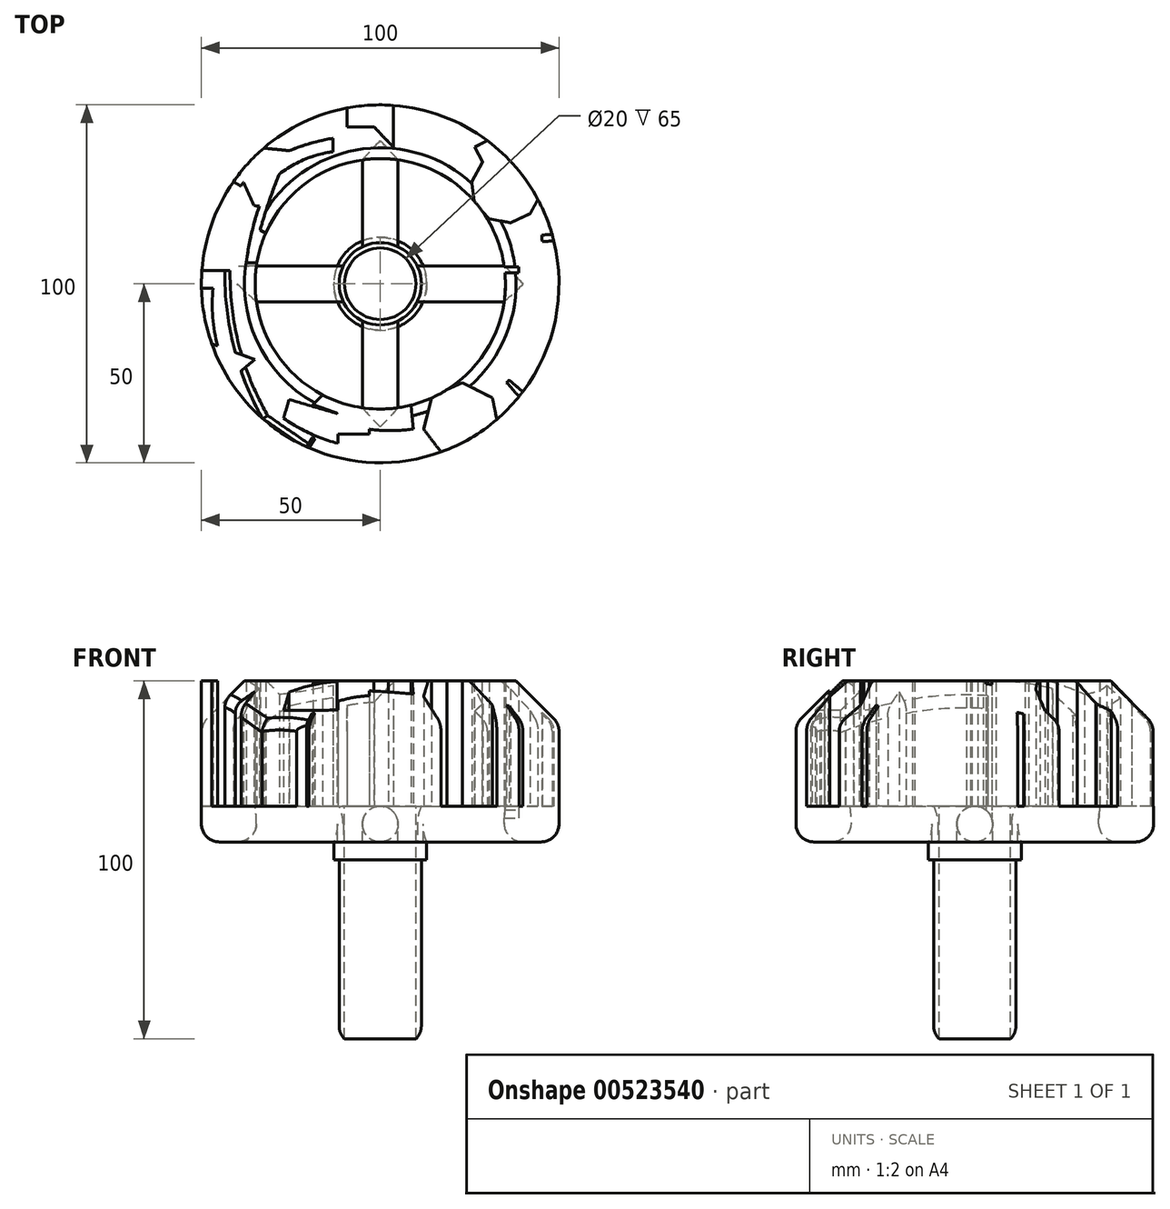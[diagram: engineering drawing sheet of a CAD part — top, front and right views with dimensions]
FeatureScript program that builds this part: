
annotation { "Feature Type Name" : "Feature", "Feature Type Description" : "" }
export const myFeature = defineFeature(function(context is Context, id is Id, definition is map)
    precondition{}
    {
        {
            var Q0;
            Q0=qCreatedBy(makeId("Top.planeOp"),FACE);
            var sketch = newSketch(context, id + "F0", { "sketchPlane" : qUnion([Q0])});
            skCircle(sketch, "E0", {"center": v(0, 0) * mm, "radius": 50 * mm});
            skArc(sketch, "E1", {"start": v(-1.78, 34.95) * mm, "mid": v(-24.53, 24.96) * mm, "end": v(-34.92, 2.39) * mm});
            skArc(sketch, "E2.trimOffspring", {"start": v(34.99, 0.84) * mm, "mid": v(25.27, 24.22) * mm, "end": v(2.33, 34.92) * mm});
            skArc(sketch, "E3.trimOffspring", {"start": v(2.06, -34.94) * mm, "mid": v(25.17, -24.32) * mm, "end": v(34.99, -0.84) * mm});
            skArc(sketch, "E4.trimOffspring", {"start": v(-34.92, -2.39) * mm, "mid": v(-24.63, -24.87) * mm, "end": v(-2.06, -34.94) * mm});
            skLineSegment(sketch, "E5", {"start": v(-2.06, -34.94) * mm, "end": v(2.06, -34.94) * mm});
            skLineSegment(sketch, "E6", {"start": v(-34.92, 2.39) * mm, "end": v(-34.92, -2.39) * mm});
            skLineSegment(sketch, "E7", {"start": v(-1.78, 34.95) * mm, "end": v(2.33, 34.92) * mm});
            skLineSegment(sketch, "E8", {"start": v(34.99, 0.84) * mm, "end": v(34.99, -0.84) * mm});
            skLineSegment(sketch, "E9", {"start": v(-49.98, -1.23) * mm, "end": v(-46.76, -1.23) * mm});
            skArc(sketch, "E10", {"start": v(-46.76, -1.23) * mm, "mid": v(-41.77, -26.37) * mm, "end": v(-23.36, -44.2) * mm});
            skLineSegment(sketch, "E11", {"start": v(-23.36, -44.2) * mm, "end": v(-33, -37.57) * mm});
            skArc(sketch, "E12", {"start": v(-43.46, 3.7) * mm, "mid": v(-40.95, -17.62) * mm, "end": v(-33, -37.57) * mm});
            skLineSegment(sketch, "E13", {"start": v(-43.46, 3.7) * mm, "end": v(-49.86, 3.7) * mm});
            skLineSegment(sketch, "E14", {"start": v(-34.5, 5.89) * mm, "end": v(-37.45, 5.89) * mm});
            skArc(sketch, "E15", {"start": v(-27.87, 34.5) * mm, "mid": v(-34.13, 20.68) * mm, "end": v(-37.45, 5.89) * mm});
            skLineSegment(sketch, "E16", {"start": v(-27.87, 34.5) * mm, "end": v(-26.89, 33.86) * mm});
            skArc(sketch, "E17", {"start": v(-26.89, 33.86) * mm, "mid": v(-30.56, 24.58) * mm, "end": v(-33.58, 15.06) * mm});
            skCircle(sketch, "E18.cCircle", {"center": v(-53.63, -24.39) * mm, "radius": 9.4 * mm, "construction": true});
            skLineSegment(sketch, "E18.0", {"start": v(-65.67, -9.96) * mm, "end": v(-35.11, -21.18) * mm});
            skLineSegment(sketch, "E18.1", {"start": v(-35.11, -21.18) * mm, "end": v(-60.11, -42.04) * mm});
            skLineSegment(sketch, "E18.2", {"start": v(-60.11, -42.04) * mm, "end": v(-65.67, -9.96) * mm});
            skPoint(sketch, "E18.0.midPoint", {"position": v(-50.4, -15.57) * mm});
            skLineSegment(sketch, "E19", {"start": v(-16.11, -31.07) * mm, "end": v(-18.86, -33.81) * mm});
            skLineSegment(sketch, "E20", {"start": v(-12.1, -36.16) * mm, "end": v(-12.12, -36.25) * mm});
            skLineSegment(sketch, "E21", {"start": v(-12.12, -36.25) * mm, "end": v(-25.48, -32.32) * mm});
            skLineSegment(sketch, "E22", {"start": v(-25.48, -32.32) * mm, "end": v(-27.02, -37.57) * mm});
            skArc(sketch, "E23", {"start": v(-27.02, -37.57) * mm, "mid": v(-19.74, -41.77) * mm, "end": v(-11.82, -44.6) * mm});
            skLineSegment(sketch, "E24", {"start": v(-11.82, -44.6) * mm, "end": v(-11.82, -42.04) * mm});
            skArc(sketch, "E25", {"start": v(-3.02, -42.04) * mm, "mid": v(-7.42, -41.96) * mm, "end": v(-11.82, -42.04) * mm});
            skLineSegment(sketch, "E26", {"start": v(-3.02, -42.04) * mm, "end": v(-3.02, -40.66) * mm});
            skArc(sketch, "E27", {"start": v(-3.02, -40.66) * mm, "mid": v(2.86, -41.04) * mm, "end": v(8.75, -40.66) * mm});
            skLineSegment(sketch, "E28", {"start": v(8.75, -40.66) * mm, "end": v(9.25, -40.6) * mm});
            skLineSegment(sketch, "E29", {"start": v(9.25, -40.6) * mm, "end": v(8.61, -33.92) * mm});
            skCircle(sketch, "E30.cCircle", {"center": v(22.75, -38.46) * mm, "radius": 9.76 * mm, "construction": true});
            skLineSegment(sketch, "E30.0", {"start": v(14.45, -31.5) * mm, "end": v(23.01, -27.63) * mm});
            skLineSegment(sketch, "E30.1", {"start": v(23.01, -27.63) * mm, "end": v(31.38, -31.91) * mm});
            skLineSegment(sketch, "E30.2", {"start": v(31.38, -31.91) * mm, "end": v(33.25, -41.13) * mm});
            skLineSegment(sketch, "E30.3", {"start": v(33.25, -41.13) * mm, "end": v(27.21, -48.33) * mm});
            skLineSegment(sketch, "E30.4", {"start": v(27.21, -48.33) * mm, "end": v(17.81, -48.1) * mm});
            skLineSegment(sketch, "E30.5", {"start": v(17.81, -48.1) * mm, "end": v(12.13, -40.62) * mm});
            skLineSegment(sketch, "E30.6", {"start": v(12.13, -40.62) * mm, "end": v(14.45, -31.5) * mm});
            skPoint(sketch, "E30.0.midPoint", {"position": v(18.73, -29.57) * mm});
            skLineSegment(sketch, "E31", {"start": v(38.83, -31.5) * mm, "end": v(35.35, -27.6) * mm});
            skLineSegment(sketch, "E32", {"start": v(35.35, -27.6) * mm, "end": v(36.1, -26.95) * mm});
            skLineSegment(sketch, "E33", {"start": v(36.1, -26.95) * mm, "end": v(39.87, -30.17) * mm});
            skLineSegment(sketch, "E34", {"start": v(30.47, -17.23) * mm, "end": v(35.47, -21.23) * mm});
            skArc(sketch, "E35", {"start": v(35.47, -21.23) * mm, "mid": v(42.73, -5.4) * mm, "end": v(45.28, 11.83) * mm});
            skLineSegment(sketch, "E36", {"start": v(45.28, 11.83) * mm, "end": v(41.92, 11.83) * mm});
            skArc(sketch, "E37", {"start": v(35.39, -16.86) * mm, "mid": v(40.36, -2.9) * mm, "end": v(41.92, 11.83) * mm});
            skLineSegment(sketch, "E38", {"start": v(35.39, -16.86) * mm, "end": v(34.06, -15.54) * mm});
            skLineSegment(sketch, "E39", {"start": v(34.06, -15.54) * mm, "end": v(37.84, -9.03) * mm});
            skLineSegment(sketch, "E40", {"start": v(37.84, -9.03) * mm, "end": v(37.84, -7.43) * mm});
            skLineSegment(sketch, "E41", {"start": v(34.95, -12.63) * mm, "end": v(37.84, -7.43) * mm});
            skLineSegment(sketch, "E42", {"start": v(34.95, -12.63) * mm, "end": v(33.03, -11.56) * mm});
            skLineSegment(sketch, "E43", {"start": v(34.86, 3.09) * mm, "end": v(38.72, 3.09) * mm});
            skLineSegment(sketch, "E44", {"start": v(38.72, 3.09) * mm, "end": v(38.72, 4.72) * mm});
            skLineSegment(sketch, "E45", {"start": v(38.72, 4.72) * mm, "end": v(34.68, 4.72) * mm});
            skCircle(sketch, "E46.cCircle", {"center": v(35.24, 26.76) * mm, "radius": 9.31 * mm, "construction": true});
            skLineSegment(sketch, "E46.0", {"start": v(30.51, 18.19) * mm, "end": v(26.37, 22.6) * mm});
            skLineSegment(sketch, "E46.1", {"start": v(26.37, 22.6) * mm, "end": v(25.62, 28.6) * mm});
            skLineSegment(sketch, "E46.2", {"start": v(25.62, 28.6) * mm, "end": v(28.54, 33.9) * mm});
            skLineSegment(sketch, "E46.3", {"start": v(28.54, 33.9) * mm, "end": v(34.02, 36.48) * mm});
            skLineSegment(sketch, "E46.4", {"start": v(34.02, 36.48) * mm, "end": v(39.96, 35.34) * mm});
            skLineSegment(sketch, "E46.5", {"start": v(39.96, 35.34) * mm, "end": v(44.1, 30.93) * mm});
            skLineSegment(sketch, "E46.6", {"start": v(44.1, 30.93) * mm, "end": v(44.85, 24.92) * mm});
            skLineSegment(sketch, "E46.7", {"start": v(44.85, 24.92) * mm, "end": v(41.93, 19.62) * mm});
            skLineSegment(sketch, "E46.8", {"start": v(41.93, 19.62) * mm, "end": v(36.45, 17.05) * mm});
            skLineSegment(sketch, "E46.9", {"start": v(36.45, 17.05) * mm, "end": v(30.51, 18.19) * mm});
            skPoint(sketch, "E46.0.midPoint", {"position": v(28.44, 20.4) * mm});
            skLineSegment(sketch, "E47", {"start": v(48.07, 13.77) * mm, "end": v(45.2, 13.64) * mm});
            skLineSegment(sketch, "E48", {"start": v(45.2, 13.64) * mm, "end": v(45.28, 11.83) * mm});
            skLineSegment(sketch, "E49", {"start": v(45.28, 11.83) * mm, "end": v(48.55, 11.97) * mm});
            skLineSegment(sketch, "E50", {"start": v(-19.9, -45.87) * mm, "end": v(-18.35, -43.34) * mm});
            skLineSegment(sketch, "E51", {"start": v(-18.35, -43.34) * mm, "end": v(-19.02, -42.93) * mm});
            skLineSegment(sketch, "E52", {"start": v(-19.02, -42.93) * mm, "end": v(-20.63, -45.55) * mm});
            skLineSegment(sketch, "E53", {"start": v(-44.57, -22.67) * mm, "end": v(-39.5, -20.05) * mm});
            skLineSegment(sketch, "E54", {"start": v(-39.5, -20.05) * mm, "end": v(-38.87, -21.26) * mm});
            skLineSegment(sketch, "E55", {"start": v(-38.87, -21.26) * mm, "end": v(-43.94, -23.87) * mm});
            skCircle(sketch, "E56.cCircle", {"center": v(-29.85, 29.47) * mm, "radius": 8.14 * mm, "construction": true});
            skLineSegment(sketch, "E56.0", {"start": v(-39.2, 30.41) * mm, "end": v(-33.7, 38.04) * mm});
            skLineSegment(sketch, "E56.1", {"start": v(-33.7, 38.04) * mm, "end": v(-24.36, 37.1) * mm});
            skLineSegment(sketch, "E56.2", {"start": v(-24.36, 37.1) * mm, "end": v(-20.5, 28.53) * mm});
            skLineSegment(sketch, "E56.3", {"start": v(-20.5, 28.53) * mm, "end": v(-25.99, 20.9) * mm});
            skLineSegment(sketch, "E56.4", {"start": v(-25.99, 20.9) * mm, "end": v(-35.33, 21.85) * mm});
            skLineSegment(sketch, "E56.5", {"start": v(-35.33, 21.85) * mm, "end": v(-39.2, 30.41) * mm});
            skPoint(sketch, "E56.0.midPoint", {"position": v(-36.45, 34.22) * mm});
            skLineSegment(sketch, "E57", {"start": v(-33.58, 15.06) * mm, "end": v(-32.05, 14.06) * mm});
            skLineSegment(sketch, "E58", {"start": v(-41.09, 28.5) * mm, "end": v(-39.05, 27.37) * mm});
            skLineSegment(sketch, "E59", {"start": v(-39.05, 27.37) * mm, "end": v(-37.54, 29.27) * mm});
            skLineSegment(sketch, "E60", {"start": v(-37.54, 29.27) * mm, "end": v(-36.54, 30.4) * mm});
            skLineSegment(sketch, "E61", {"start": v(-36.54, 30.4) * mm, "end": v(-37.26, 31.03) * mm});
            skLineSegment(sketch, "E62", {"start": v(-37.26, 31.03) * mm, "end": v(-39.1, 28.93) * mm});
            skLineSegment(sketch, "E63", {"start": v(-39.1, 28.93) * mm, "end": v(-40.53, 29.28) * mm});
            skLineSegment(sketch, "E64", {"start": v(34.45, 22.66) * mm, "end": v(21.46, 43.14) * mm});
            skLineSegment(sketch, "E65", {"start": v(27.1, 39.14) * mm, "end": v(21.46, 43.14) * mm});
            skLineSegment(sketch, "E66", {"start": v(3.7, 38.31) * mm, "end": v(3.7, 49.86) * mm});
            skArc(sketch, "E67", {"start": v(-5.98, 49.5) * mm, "mid": v(-1.45, 43.64) * mm, "end": v(3.7, 38.31) * mm});
            skLineSegment(sketch, "E68", {"start": v(3.36, 49.89) * mm, "end": v(8.72, 49.5) * mm});
            skLineSegment(sketch, "E69", {"start": v(8.72, 49.5) * mm, "end": v(12.9, 46.7) * mm});
            skArc(sketch, "E70", {"start": v(12.42, 39.14) * mm, "mid": v(12.75, 42.9) * mm, "end": v(12.9, 46.7) * mm});
            skLineSegment(sketch, "E71", {"start": v(12.42, 39.14) * mm, "end": v(18.31, 46.33) * mm});
            skLineSegment(sketch, "E72", {"start": v(18.31, 46.33) * mm, "end": v(27.1, 39.14) * mm});
            skLineSegment(sketch, "E73", {"start": v(33.6, 24.3) * mm, "end": v(44.87, 30.1) * mm});
            skLineSegment(sketch, "E74", {"start": v(26.6, 37.9) * mm, "end": v(33.6, 24.3) * mm});
            skLineSegment(sketch, "E75", {"start": v(26.45, 38.2) * mm, "end": v(29.98, 40.01) * mm});
            skLineSegment(sketch, "E76", {"start": v(-6.34, 49.6) * mm, "end": v(-6.34, 45.67) * mm});
            skLineSegment(sketch, "E77", {"start": v(-6.34, 45.67) * mm, "end": v(2.1, 45.67) * mm});
            skLineSegment(sketch, "E78", {"start": v(2.1, 45.67) * mm, "end": v(2.1, 43.86) * mm});
            skLineSegment(sketch, "E79", {"start": v(2.1, 43.86) * mm, "end": v(-4.7, 43.86) * mm});
            skLineSegment(sketch, "E80", {"start": v(-4.7, 43.86) * mm, "end": v(-9.23, 43.86) * mm});
            skLineSegment(sketch, "E81", {"start": v(-9.23, 43.86) * mm, "end": v(-9.23, 49.14) * mm});
            skArc(sketch, "E82", {"start": v(-13.2, 36.91) * mm, "mid": v(-32.08, 27.2) * mm, "end": v(-40.55, 7.74) * mm});
            skLineSegment(sketch, "E83", {"start": v(-13.2, 36.91) * mm, "end": v(-13.2, 40.67) * mm});
            skArc(sketch, "E84", {"start": v(-13.2, 40.67) * mm, "mid": v(-23.19, 38.06) * mm, "end": v(-32.5, 33.6) * mm});
            skLineSegment(sketch, "E85.trimOffspring", {"start": v(26.45, 38.2) * mm, "end": v(34.45, 22.66) * mm});
            skLineSegment(sketch, "E86", {"start": v(-18.86, -33.81) * mm, "end": v(-12.1, -36.16) * mm});
            skSolve(sketch);
        }
        {
            var Q0;
            Q0=qCreatedBy(makeId("Top.planeOp"),FACE);
            var sketch = newSketch(context, id + "F1", { "sketchPlane" : qUnion([Q0])});
            skCircle(sketch, "E87", {"center": v(0, 0) * mm, "radius": 10 * mm});
            skArc(sketch, "E88", {"start": v(-10.36, -5) * mm, "mid": v(-8.13, -8.13) * mm, "end": v(-5, -10.36) * mm});
            skCircle(sketch, "E89", {"center": v(0, 0) * mm, "radius": 50 * mm});
            skArc(sketch, "E90", {"start": v(-34.64, -5) * mm, "mid": v(-24.75, -24.75) * mm, "end": v(-5, -34.64) * mm});
            skLineSegment(sketch, "E91", {"start": v(-5, 34.64) * mm, "end": v(-5, 10.36) * mm});
            skLineSegment(sketch, "E92", {"start": v(5, 10.36) * mm, "end": v(5, 34.64) * mm});
            skLineSegment(sketch, "E93.MirrorCS", {"start": v(10.36, 5) * mm, "end": v(34.64, 5) * mm});
            skLineSegment(sketch, "E94.MirrorCS", {"start": v(10.36, -5) * mm, "end": v(34.64, -5) * mm});
            skLineSegment(sketch, "E95.MirrorCS", {"start": v(5, -10.36) * mm, "end": v(5, -34.64) * mm});
            skLineSegment(sketch, "E96.MirrorCS", {"start": v(-5, -34.64) * mm, "end": v(-5, -10.36) * mm});
            skLineSegment(sketch, "E97.MirrorCS", {"start": v(-10.36, 5) * mm, "end": v(-34.64, 5) * mm});
            skLineSegment(sketch, "E98.MirrorCS", {"start": v(-10.36, -5) * mm, "end": v(-34.64, -5) * mm});
            skArc(sketch, "E99.trimOffspring", {"start": v(-5, 10.36) * mm, "mid": v(-8.13, 8.13) * mm, "end": v(-10.36, 5) * mm});
            skArc(sketch, "E100.trimOffspring", {"start": v(10.36, 5) * mm, "mid": v(8.13, 8.13) * mm, "end": v(5, 10.36) * mm});
            skArc(sketch, "E101.trimOffspring", {"start": v(5, -10.36) * mm, "mid": v(8.13, -8.13) * mm, "end": v(10.36, -5) * mm});
            skArc(sketch, "E102.trimOffspring", {"start": v(34.64, 5) * mm, "mid": v(24.75, 24.75) * mm, "end": v(5, 34.64) * mm});
            skArc(sketch, "E103.trimOffspring", {"start": v(5, -34.64) * mm, "mid": v(24.75, -24.75) * mm, "end": v(34.64, -5) * mm});
            skArc(sketch, "E104.trimOffspring", {"start": v(-5, 34.64) * mm, "mid": v(-24.75, 24.75) * mm, "end": v(-34.64, 5) * mm});
            skSolve(sketch);
        }
        {
            var Q0;
            Q0=qCreatedBy(makeId("Top.planeOp"),FACE);
            var sketch = newSketch(context, id + "F2", { "sketchPlane" : qUnion([Q0])});
            skCircle(sketch, "E105", {"center": v(0, 0) * mm, "radius": 11.5 * mm});
            skCircle(sketch, "E106", {"center": v(0, 0) * mm, "radius": 13 * mm});
            skSolve(sketch);
        }
        {
            var Q0;
            Q0=makeQuery(id+"F1.imprint","IMPRINT",FACE,{"disambiguationData":[TD([[makeQuery(id+"F1.imprint","IMPRINT",EDGE,{"derivedFrom":sQuery(id+"F1.wireOp",EDGE,"E87")}),-1.0]])]});
            var sketch = newSketch(context, id + "F3", { "sketchPlane" : qUnion([Q0])});
            skCircle(sketch, "E107", {"center": v(0, 0) * mm, "radius": 10 * mm});
            skCircle(sketch, "E108", {"center": v(0, 0) * mm, "radius": 11.5 * mm});
            skSolve(sketch);
        }
        {
            var Q0;
            Q0=makeQuery(id+"F2.imprint","IMPRINT",FACE,{"disambiguationData":[TD([[makeQuery(id+"F2.imprint","IMPRINT",EDGE,{"derivedFrom":sQuery(id+"F2.wireOp",EDGE,"E105")}),-1.0]])]});
            extrude(context, id + "F4", {"entities" : qUnion([Q0]), "oppositeDirection" : true, "depth" : 5 * mm, "offsetDistance" : 25 * mm});
        }
        {
            var Q0;
            Q0=makeQuery(id+"F3.imprint","IMPRINT",FACE,{"disambiguationData":[TD([[makeQuery(id+"F3.imprint","IMPRINT",EDGE,{"derivedFrom":sQuery(id+"F3.wireOp",EDGE,"E107")}),-1.0]])]});
            extrude(context, id + "F5", {"entities" : qUnion([Q0]), "operationType" : NewBodyOperationType.ADD, "oppositeDirection" : true, "depth" : 55 * mm, "offsetDistance" : 25 * mm});
        }
        {
            var Q0;
            Q0=makeQuery(id+"F1.imprint","IMPRINT",FACE,{"disambiguationData":[TD([[makeQuery(id+"F1.imprint","IMPRINT",EDGE,{"derivedFrom":sQuery(id+"F1.wireOp",EDGE,"E87")}),-1.0]])]});
            extrude(context, id + "F6", {"entities" : qUnion([Q0]), "operationType" : NewBodyOperationType.ADD, "depth" : 10 * mm, "offsetDistance" : 25 * mm});
        }
        {
            var Q0;
            {var subQ3=sQuery(id+"F0.wireOp",EDGE,"E30.1");Q0=makeQuery(id+"F0.imprint","IMPRINT",FACE,{"disambiguationData":[TD([[makeQuery(id+"F0.imprint","IMPRINT",EDGE,{"derivedFrom":subQ3}),1.0]])]});}
            var Q1;
            {var subQ0=sQuery(id+"F0.wireOp",EDGE,"E8");Q1=makeQuery(id+"F0.imprint","IMPRINT",FACE,{"disambiguationData":[TD([[makeQuery(id+"F0.imprint","IMPRINT",EDGE,{"derivedFrom":subQ0}),1.0]])]});}
            var Q2;
            {var subQ0=sQuery(id+"F0.wireOp",EDGE,"E34");Q2=makeQuery(id+"F0.imprint","IMPRINT",FACE,{"disambiguationData":[TD([[makeQuery(id+"F0.imprint","IMPRINT",EDGE,{"derivedFrom":subQ0}),1.0]])]});}
            var Q3;
            {var subQ12=sQuery(id+"F0.wireOp",EDGE,"E6");Q3=makeQuery(id+"F0.imprint","IMPRINT",FACE,{"disambiguationData":[TD([[makeQuery(id+"F0.imprint","IMPRINT",EDGE,{"derivedFrom":subQ12}),-1.0]])]});}
            var Q4;
            {var subQ0=sQuery(id+"F0.wireOp",EDGE,"E9");Q4=makeQuery(id+"F0.imprint","IMPRINT",FACE,{"disambiguationData":[TD([[makeQuery(id+"F0.imprint","IMPRINT",EDGE,{"derivedFrom":subQ0}),-1.0]])]});}
            var Q5;
            {var subQ14=sQuery(id+"F0.wireOp",EDGE,"E7");Q5=makeQuery(id+"F0.imprint","IMPRINT",FACE,{"disambiguationData":[TD([[makeQuery(id+"F0.imprint","IMPRINT",EDGE,{"derivedFrom":subQ14}),1.0]])]});}
            var Q6;
            {var subQ0=sQuery(id+"F0.wireOp",EDGE,"E56.3");var subQ3=sQuery(id+"F0.wireOp",EDGE,"E1");var subQ4=makeQuery(id+"F0.imprint","INTERSECT",VERTEX,{"derivedFrom":[subQ3,subQ0]});Q6=makeQuery(id+"F0.imprint","IMPRINT",FACE,{"disambiguationData":[TD([[makeQuery(id+"F0.imprint","IMPRINT",EDGE,{"disambiguationData":[TD([[subQ4,-1.0]])],"derivedFrom":subQ3}),-1.0]])]});}
            var Q7;
            {var subQ5=sQuery(id+"F0.wireOp",EDGE,"E65");Q7=makeQuery(id+"F0.imprint","IMPRINT",FACE,{"disambiguationData":[TD([[makeQuery(id+"F0.imprint","IMPRINT",EDGE,{"derivedFrom":subQ5}),1.0]])]});}
            var Q8;
            {var subQ0=sQuery(id+"F0.wireOp",EDGE,"E57");Q8=makeQuery(id+"F0.imprint","IMPRINT",FACE,{"disambiguationData":[TD([[makeQuery(id+"F0.imprint","IMPRINT",EDGE,{"derivedFrom":subQ0}),1.0]])]});}
            extrude(context, id + "F7", {"entities" : qUnion([Q0, Q1, Q2, Q3, Q4, Q5, Q6, Q7, Q8]), "operationType" : NewBodyOperationType.ADD, "depth" : 45 * mm, "offsetDistance" : 25 * mm});
        }
        {
            var Q0;
            {var subQ0=sQuery(id+"F0.wireOp",EDGE,"E0");Q0=makeQuery(id+"F7.opExtrude","CAP_EDGE",EDGE,{"disambiguationData":[OSD([subQ0]),TDD([makeQuery(id+"F0.imprint","IMPRINT",EDGE,{"disambiguationData":[TD([[makeQuery(id+"F0.imprint","INTERSECT",VERTEX,{"derivedFrom":[subQ0,sQuery(id+"F0.wireOp",EDGE,"E33")]}),-1.0]])],"derivedFrom":subQ0})])],"isStart":false});}
            var Q1;
            {var subQ0=sQuery(id+"F0.wireOp",EDGE,"E0");Q1=makeQuery(id+"F7.opExtrude","CAP_EDGE",EDGE,{"disambiguationData":[OSD([subQ0]),TDD([makeQuery(id+"F0.imprint","IMPRINT",EDGE,{"disambiguationData":[TD([[makeQuery(id+"F0.imprint","INTERSECT",VERTEX,{"derivedFrom":[subQ0,sQuery(id+"F0.wireOp",EDGE,"E81")]}),-1.0]])],"derivedFrom":subQ0})])],"isStart":false});}
            var Q2;
            {var subQ0=sQuery(id+"F0.wireOp",EDGE,"E0");Q2=makeQuery(id+"F7.opExtrude","CAP_EDGE",EDGE,{"disambiguationData":[OSD([subQ0]),TDD([makeQuery(id+"F0.imprint","IMPRINT",EDGE,{"disambiguationData":[TD([[makeQuery(id+"F0.imprint","INTERSECT",VERTEX,{"derivedFrom":[subQ0,sQuery(id+"F0.wireOp",EDGE,"E13")]}),1.0]])],"derivedFrom":subQ0})])],"isStart":false});}
            chamfer(context, id + "F8", {"entities" : qUnion([Q0, Q1, Q2]), "width" : 12 * mm, "tangentPropagation" : true});
        }
        {
            var Q0;
            Q0=makeQuery(id+"F6.opExtrude","CAP_EDGE",EDGE,{"disambiguationData":[OSD([sQuery(id+"F1.wireOp",EDGE,"E89")])],"isStart":true});
            var Q1;
            Q1=makeQuery(id+"F5.opExtrude","CAP_EDGE",EDGE,{"disambiguationData":[OSD([sQuery(id+"F3.wireOp",EDGE,"E108")])],"isStart":false});
            fillet(context, id + "F9", {"entities" : qUnion([Q0, Q1]), "radius" : 5 * mm, "tangentPropagation" : true, "allowEdgeOverflow" : false});
        }
        {
            var Q0;
            {var subQ0=sQuery(id+"F1.wireOp",EDGE,"E94.MirrorCS");Q0=makeQuery(id+"F6.boolean.opBoolean","SPLIT",EDGE,{"disambiguationData":[topologyDisambiguationEdgeConnected([makeQuery(id+"F6.opExtrude","CAP_FACE",FACE,{"disambiguationData":[OSD([sQuery(id+"F1.wireOp",EDGE,"E87"),sQuery(id+"F1.wireOp",EDGE,"E88"),sQuery(id+"F1.wireOp",EDGE,"E89"),sQuery(id+"F1.wireOp",EDGE,"E90"),sQuery(id+"F1.wireOp",EDGE,"E91"),sQuery(id+"F1.wireOp",EDGE,"E92"),sQuery(id+"F1.wireOp",EDGE,"E93.MirrorCS"),subQ0,sQuery(id+"F1.wireOp",EDGE,"E95.MirrorCS"),sQuery(id+"F1.wireOp",EDGE,"E96.MirrorCS"),sQuery(id+"F1.wireOp",EDGE,"E97.MirrorCS"),sQuery(id+"F1.wireOp",EDGE,"E98.MirrorCS"),sQuery(id+"F1.wireOp",EDGE,"E99.trimOffspring"),sQuery(id+"F1.wireOp",EDGE,"E100.trimOffspring"),sQuery(id+"F1.wireOp",EDGE,"E101.trimOffspring"),sQuery(id+"F1.wireOp",EDGE,"E102.trimOffspring"),sQuery(id+"F1.wireOp",EDGE,"E103.trimOffspring"),sQuery(id+"F1.wireOp",EDGE,"E104.trimOffspring")])],"isStart":true})])],"derivedFrom":makeQuery(id+"F6.opExtrude","CAP_EDGE",EDGE,{"disambiguationData":[OSD([subQ0])],"isStart":true})});}
            var Q1;
            {var subQ0=sQuery(id+"F1.wireOp",EDGE,"E93.MirrorCS");Q1=makeQuery(id+"F6.boolean.opBoolean","SPLIT",EDGE,{"disambiguationData":[topologyDisambiguationEdgeConnected([makeQuery(id+"F6.opExtrude","CAP_FACE",FACE,{"disambiguationData":[OSD([sQuery(id+"F1.wireOp",EDGE,"E87"),sQuery(id+"F1.wireOp",EDGE,"E88"),sQuery(id+"F1.wireOp",EDGE,"E89"),sQuery(id+"F1.wireOp",EDGE,"E90"),sQuery(id+"F1.wireOp",EDGE,"E91"),sQuery(id+"F1.wireOp",EDGE,"E92"),subQ0,sQuery(id+"F1.wireOp",EDGE,"E94.MirrorCS"),sQuery(id+"F1.wireOp",EDGE,"E95.MirrorCS"),sQuery(id+"F1.wireOp",EDGE,"E96.MirrorCS"),sQuery(id+"F1.wireOp",EDGE,"E97.MirrorCS"),sQuery(id+"F1.wireOp",EDGE,"E98.MirrorCS"),sQuery(id+"F1.wireOp",EDGE,"E99.trimOffspring"),sQuery(id+"F1.wireOp",EDGE,"E100.trimOffspring"),sQuery(id+"F1.wireOp",EDGE,"E101.trimOffspring"),sQuery(id+"F1.wireOp",EDGE,"E102.trimOffspring"),sQuery(id+"F1.wireOp",EDGE,"E103.trimOffspring"),sQuery(id+"F1.wireOp",EDGE,"E104.trimOffspring")])],"isStart":true})])],"derivedFrom":makeQuery(id+"F6.opExtrude","CAP_EDGE",EDGE,{"disambiguationData":[OSD([subQ0])],"isStart":true})});}
            var Q2;
            {var subQ0=sQuery(id+"F1.wireOp",EDGE,"E95.MirrorCS");Q2=makeQuery(id+"F6.boolean.opBoolean","SPLIT",EDGE,{"disambiguationData":[topologyDisambiguationEdgeConnected([makeQuery(id+"F6.opExtrude","CAP_FACE",FACE,{"disambiguationData":[OSD([sQuery(id+"F1.wireOp",EDGE,"E87"),sQuery(id+"F1.wireOp",EDGE,"E88"),sQuery(id+"F1.wireOp",EDGE,"E89"),sQuery(id+"F1.wireOp",EDGE,"E90"),sQuery(id+"F1.wireOp",EDGE,"E91"),sQuery(id+"F1.wireOp",EDGE,"E92"),sQuery(id+"F1.wireOp",EDGE,"E93.MirrorCS"),sQuery(id+"F1.wireOp",EDGE,"E94.MirrorCS"),subQ0,sQuery(id+"F1.wireOp",EDGE,"E96.MirrorCS"),sQuery(id+"F1.wireOp",EDGE,"E97.MirrorCS"),sQuery(id+"F1.wireOp",EDGE,"E98.MirrorCS"),sQuery(id+"F1.wireOp",EDGE,"E99.trimOffspring"),sQuery(id+"F1.wireOp",EDGE,"E100.trimOffspring"),sQuery(id+"F1.wireOp",EDGE,"E101.trimOffspring"),sQuery(id+"F1.wireOp",EDGE,"E102.trimOffspring"),sQuery(id+"F1.wireOp",EDGE,"E103.trimOffspring"),sQuery(id+"F1.wireOp",EDGE,"E104.trimOffspring")])],"isStart":true})])],"derivedFrom":makeQuery(id+"F6.opExtrude","CAP_EDGE",EDGE,{"disambiguationData":[OSD([subQ0])],"isStart":true})});}
            var Q3;
            {var subQ0=sQuery(id+"F1.wireOp",EDGE,"E96.MirrorCS");Q3=makeQuery(id+"F6.boolean.opBoolean","SPLIT",EDGE,{"disambiguationData":[topologyDisambiguationEdgeConnected([makeQuery(id+"F6.opExtrude","CAP_FACE",FACE,{"disambiguationData":[OSD([sQuery(id+"F1.wireOp",EDGE,"E87"),sQuery(id+"F1.wireOp",EDGE,"E88"),sQuery(id+"F1.wireOp",EDGE,"E89"),sQuery(id+"F1.wireOp",EDGE,"E90"),sQuery(id+"F1.wireOp",EDGE,"E91"),sQuery(id+"F1.wireOp",EDGE,"E92"),sQuery(id+"F1.wireOp",EDGE,"E93.MirrorCS"),sQuery(id+"F1.wireOp",EDGE,"E94.MirrorCS"),sQuery(id+"F1.wireOp",EDGE,"E95.MirrorCS"),subQ0,sQuery(id+"F1.wireOp",EDGE,"E97.MirrorCS"),sQuery(id+"F1.wireOp",EDGE,"E98.MirrorCS"),sQuery(id+"F1.wireOp",EDGE,"E99.trimOffspring"),sQuery(id+"F1.wireOp",EDGE,"E100.trimOffspring"),sQuery(id+"F1.wireOp",EDGE,"E101.trimOffspring"),sQuery(id+"F1.wireOp",EDGE,"E102.trimOffspring"),sQuery(id+"F1.wireOp",EDGE,"E103.trimOffspring"),sQuery(id+"F1.wireOp",EDGE,"E104.trimOffspring")])],"isStart":true})])],"derivedFrom":makeQuery(id+"F6.opExtrude","CAP_EDGE",EDGE,{"disambiguationData":[OSD([subQ0])],"isStart":true})});}
            var Q4;
            {var subQ0=sQuery(id+"F1.wireOp",EDGE,"E92");Q4=makeQuery(id+"F6.boolean.opBoolean","SPLIT",EDGE,{"disambiguationData":[topologyDisambiguationEdgeConnected([makeQuery(id+"F6.opExtrude","CAP_FACE",FACE,{"disambiguationData":[OSD([sQuery(id+"F1.wireOp",EDGE,"E87"),sQuery(id+"F1.wireOp",EDGE,"E88"),sQuery(id+"F1.wireOp",EDGE,"E89"),sQuery(id+"F1.wireOp",EDGE,"E90"),sQuery(id+"F1.wireOp",EDGE,"E91"),subQ0,sQuery(id+"F1.wireOp",EDGE,"E93.MirrorCS"),sQuery(id+"F1.wireOp",EDGE,"E94.MirrorCS"),sQuery(id+"F1.wireOp",EDGE,"E95.MirrorCS"),sQuery(id+"F1.wireOp",EDGE,"E96.MirrorCS"),sQuery(id+"F1.wireOp",EDGE,"E97.MirrorCS"),sQuery(id+"F1.wireOp",EDGE,"E98.MirrorCS"),sQuery(id+"F1.wireOp",EDGE,"E99.trimOffspring"),sQuery(id+"F1.wireOp",EDGE,"E100.trimOffspring"),sQuery(id+"F1.wireOp",EDGE,"E101.trimOffspring"),sQuery(id+"F1.wireOp",EDGE,"E102.trimOffspring"),sQuery(id+"F1.wireOp",EDGE,"E103.trimOffspring"),sQuery(id+"F1.wireOp",EDGE,"E104.trimOffspring")])],"isStart":true})])],"derivedFrom":makeQuery(id+"F6.opExtrude","CAP_EDGE",EDGE,{"disambiguationData":[OSD([subQ0])],"isStart":true})});}
            var Q5;
            {var subQ0=sQuery(id+"F1.wireOp",EDGE,"E91");Q5=makeQuery(id+"F6.boolean.opBoolean","SPLIT",EDGE,{"disambiguationData":[topologyDisambiguationEdgeConnected([makeQuery(id+"F6.opExtrude","CAP_FACE",FACE,{"disambiguationData":[OSD([sQuery(id+"F1.wireOp",EDGE,"E87"),sQuery(id+"F1.wireOp",EDGE,"E88"),sQuery(id+"F1.wireOp",EDGE,"E89"),sQuery(id+"F1.wireOp",EDGE,"E90"),subQ0,sQuery(id+"F1.wireOp",EDGE,"E92"),sQuery(id+"F1.wireOp",EDGE,"E93.MirrorCS"),sQuery(id+"F1.wireOp",EDGE,"E94.MirrorCS"),sQuery(id+"F1.wireOp",EDGE,"E95.MirrorCS"),sQuery(id+"F1.wireOp",EDGE,"E96.MirrorCS"),sQuery(id+"F1.wireOp",EDGE,"E97.MirrorCS"),sQuery(id+"F1.wireOp",EDGE,"E98.MirrorCS"),sQuery(id+"F1.wireOp",EDGE,"E99.trimOffspring"),sQuery(id+"F1.wireOp",EDGE,"E100.trimOffspring"),sQuery(id+"F1.wireOp",EDGE,"E101.trimOffspring"),sQuery(id+"F1.wireOp",EDGE,"E102.trimOffspring"),sQuery(id+"F1.wireOp",EDGE,"E103.trimOffspring"),sQuery(id+"F1.wireOp",EDGE,"E104.trimOffspring")])],"isStart":true})])],"derivedFrom":makeQuery(id+"F6.opExtrude","CAP_EDGE",EDGE,{"disambiguationData":[OSD([subQ0])],"isStart":true})});}
            var Q6;
            {var subQ0=sQuery(id+"F1.wireOp",EDGE,"E98.MirrorCS");Q6=makeQuery(id+"F6.boolean.opBoolean","SPLIT",EDGE,{"disambiguationData":[topologyDisambiguationEdgeConnected([makeQuery(id+"F6.opExtrude","CAP_FACE",FACE,{"disambiguationData":[OSD([sQuery(id+"F1.wireOp",EDGE,"E87"),sQuery(id+"F1.wireOp",EDGE,"E88"),sQuery(id+"F1.wireOp",EDGE,"E89"),sQuery(id+"F1.wireOp",EDGE,"E90"),sQuery(id+"F1.wireOp",EDGE,"E91"),sQuery(id+"F1.wireOp",EDGE,"E92"),sQuery(id+"F1.wireOp",EDGE,"E93.MirrorCS"),sQuery(id+"F1.wireOp",EDGE,"E94.MirrorCS"),sQuery(id+"F1.wireOp",EDGE,"E95.MirrorCS"),sQuery(id+"F1.wireOp",EDGE,"E96.MirrorCS"),sQuery(id+"F1.wireOp",EDGE,"E97.MirrorCS"),subQ0,sQuery(id+"F1.wireOp",EDGE,"E99.trimOffspring"),sQuery(id+"F1.wireOp",EDGE,"E100.trimOffspring"),sQuery(id+"F1.wireOp",EDGE,"E101.trimOffspring"),sQuery(id+"F1.wireOp",EDGE,"E102.trimOffspring"),sQuery(id+"F1.wireOp",EDGE,"E103.trimOffspring"),sQuery(id+"F1.wireOp",EDGE,"E104.trimOffspring")])],"isStart":true})])],"derivedFrom":makeQuery(id+"F6.opExtrude","CAP_EDGE",EDGE,{"disambiguationData":[OSD([subQ0])],"isStart":true})});}
            var Q7;
            Q7=makeQuery(id+"F6.opExtrude","CAP_EDGE",EDGE,{"disambiguationData":[OSD([sQuery(id+"F1.wireOp",EDGE,"E90")])],"isStart":true});
            var Q8;
            Q8=makeQuery(id+"F6.opExtrude","CAP_EDGE",EDGE,{"disambiguationData":[OSD([sQuery(id+"F1.wireOp",EDGE,"E103.trimOffspring")])],"isStart":true});
            var Q9;
            Q9=makeQuery(id+"F6.opExtrude","CAP_EDGE",EDGE,{"disambiguationData":[OSD([sQuery(id+"F1.wireOp",EDGE,"E102.trimOffspring")])],"isStart":true});
            var Q10;
            Q10=makeQuery(id+"F6.opExtrude","CAP_EDGE",EDGE,{"disambiguationData":[OSD([sQuery(id+"F1.wireOp",EDGE,"E104.trimOffspring")])],"isStart":true});
            var Q11;
            Q11=makeQuery(id+"F6.opExtrude","CAP_EDGE",EDGE,{"disambiguationData":[OSD([sQuery(id+"F1.wireOp",EDGE,"E97.MirrorCS")])],"isStart":false});
            var Q12;
            Q12=makeQuery(id+"F6.opExtrude","CAP_EDGE",EDGE,{"disambiguationData":[OSD([sQuery(id+"F1.wireOp",EDGE,"E91")])],"isStart":false});
            var Q13;
            Q13=makeQuery(id+"F6.opExtrude","CAP_EDGE",EDGE,{"disambiguationData":[OSD([sQuery(id+"F1.wireOp",EDGE,"E92")])],"isStart":false});
            var Q14;
            Q14=makeQuery(id+"F6.opExtrude","CAP_EDGE",EDGE,{"disambiguationData":[OSD([sQuery(id+"F1.wireOp",EDGE,"E98.MirrorCS")])],"isStart":false});
            var Q15;
            Q15=makeQuery(id+"F6.opExtrude","CAP_EDGE",EDGE,{"disambiguationData":[OSD([sQuery(id+"F1.wireOp",EDGE,"E94.MirrorCS")])],"isStart":false});
            var Q16;
            Q16=makeQuery(id+"F6.opExtrude","CAP_EDGE",EDGE,{"disambiguationData":[OSD([sQuery(id+"F1.wireOp",EDGE,"E93.MirrorCS")])],"isStart":false});
            var Q17;
            Q17=makeQuery(id+"F6.opExtrude","CAP_EDGE",EDGE,{"disambiguationData":[OSD([sQuery(id+"F1.wireOp",EDGE,"E95.MirrorCS")])],"isStart":false});
            var Q18;
            Q18=makeQuery(id+"F6.opExtrude","CAP_EDGE",EDGE,{"disambiguationData":[OSD([sQuery(id+"F1.wireOp",EDGE,"E96.MirrorCS")])],"isStart":false});
            var Q19;
            {var subQ0=sQuery(id+"F0.wireOp",EDGE,"E0");var subQ1=makeQuery(id+"F0.imprint","IMPRINT",EDGE,{"disambiguationData":[TD([[makeQuery(id+"F0.imprint","INTERSECT",VERTEX,{"derivedFrom":[subQ0,sQuery(id+"F0.wireOp",EDGE,"E33")]}),-1.0]])],"derivedFrom":subQ0});var subQ2=makeQuery(id+"F0.imprint","INTERSECT",VERTEX,{"derivedFrom":[subQ0,sQuery(id+"F0.wireOp",EDGE,"E69")]});Q19=makeQuery(id+"F8.opChamfer","BLEND_EDGE",EDGE,{"disambiguationData":[OD(1.0)],"blendedFrom":[makeQuery(id+"F7.opExtrude","CAP_EDGE",EDGE,{"disambiguationData":[OSD([subQ0]),TDD([subQ1])],"isStart":false}),makeQuery(id+"F7.boolean.opBoolean","MERGE",FACE,{"derivedFrom":[makeQuery(id+"F6.opExtrude","SWEPT_FACE",FACE,{"disambiguationData":[OSD([sQuery(id+"F1.wireOp",EDGE,"E89")])]}),makeQuery(id+"F7.opExtrude","SWEPT_FACE",FACE,{"disambiguationData":[OSD([subQ0]),TDD([makeQuery(id+"F0.imprint","IMPRINT",EDGE,{"disambiguationData":[TD([[makeQuery(id+"F0.imprint","INTERSECT",VERTEX,{"derivedFrom":[subQ0,sQuery(id+"F0.wireOp",EDGE,"E47")]}),-1.0]])],"derivedFrom":subQ0})])]}),makeQuery(id+"F7.opExtrude","SWEPT_FACE",FACE,{"disambiguationData":[OSD([subQ0]),TDD([makeQuery(id+"F0.imprint","IMPRINT",EDGE,{"disambiguationData":[TD([[makeQuery(id+"F0.imprint","INTERSECT",VERTEX,{"derivedFrom":[subQ0,sQuery(id+"F0.wireOp",EDGE,"E75")]}),-1.0]])],"derivedFrom":subQ0}),makeQuery(id+"F0.imprint","IMPRINT",EDGE,{"disambiguationData":[TD([[subQ2,-1.0]])],"derivedFrom":subQ0})])]}),makeQuery(id+"F7.opExtrude","SWEPT_FACE",FACE,{"disambiguationData":[OSD([subQ0]),TDD([makeQuery(id+"F0.imprint","IMPRINT",EDGE,{"disambiguationData":[TD([[makeQuery(id+"F0.imprint","INTERSECT",VERTEX,{"derivedFrom":[subQ0,sQuery(id+"F0.wireOp",EDGE,"E81")]}),-1.0]])],"derivedFrom":subQ0})])]}),makeQuery(id+"F7.opExtrude","SWEPT_FACE",FACE,{"disambiguationData":[OSD([subQ0]),TDD([makeQuery(id+"F0.imprint","IMPRINT",EDGE,{"disambiguationData":[TD([[makeQuery(id+"F0.imprint","INTERSECT",VERTEX,{"derivedFrom":[subQ0,sQuery(id+"F0.wireOp",EDGE,"E13")]}),1.0]])],"derivedFrom":subQ0})])]}),makeQuery(id+"F7.opExtrude","SWEPT_FACE",FACE,{"disambiguationData":[OSD([subQ0]),TDD([makeQuery(id+"F0.imprint","IMPRINT",EDGE,{"disambiguationData":[TD([[makeQuery(id+"F0.imprint","INTERSECT",VERTEX,{"derivedFrom":[subQ0,sQuery(id+"F0.wireOp",EDGE,"E9")]}),-1.0]])],"derivedFrom":subQ0})])]}),makeQuery(id+"F7.opExtrude","SWEPT_FACE",FACE,{"disambiguationData":[OSD([subQ0]),TDD([makeQuery(id+"F0.imprint","IMPRINT",EDGE,{"disambiguationData":[TD([[makeQuery(id+"F0.imprint","INTERSECT",VERTEX,{"derivedFrom":[subQ0,sQuery(id+"F0.wireOp",EDGE,"E52")]}),1.0]])],"derivedFrom":subQ0})])]}),makeQuery(id+"F7.opExtrude","SWEPT_FACE",FACE,{"disambiguationData":[OSD([subQ0]),TDD([makeQuery(id+"F0.imprint","IMPRINT",EDGE,{"disambiguationData":[TD([[makeQuery(id+"F0.imprint","INTERSECT",VERTEX,{"derivedFrom":[subQ0,sQuery(id+"F0.wireOp",EDGE,"E50")]}),-1.0]])],"derivedFrom":subQ0})])]}),makeQuery(id+"F7.opExtrude","SWEPT_FACE",FACE,{"disambiguationData":[OSD([subQ0]),TDD([makeQuery(id+"F0.imprint","IMPRINT",EDGE,{"disambiguationData":[TD([[makeQuery(id+"F0.imprint","INTERSECT",VERTEX,{"derivedFrom":[subQ0,sQuery(id+"F0.wireOp",EDGE,"E31")]}),1.0]])],"derivedFrom":subQ0})])]}),makeQuery(id+"F7.opExtrude","SWEPT_FACE",FACE,{"disambiguationData":[OSD([subQ0]),TDD([subQ1])]})]})],"blendedInto":[makeQuery(id+"F7.boolean.opBoolean","MERGE",FACE,{"derivedFrom":[makeQuery(id+"F6.opExtrude","SWEPT_FACE",FACE,{"disambiguationData":[OSD([sQuery(id+"F1.wireOp",EDGE,"E89")])]}),makeQuery(id+"F7.opExtrude","SWEPT_FACE",FACE,{"disambiguationData":[OSD([subQ0]),TDD([makeQuery(id+"F0.imprint","IMPRINT",EDGE,{"disambiguationData":[TD([[makeQuery(id+"F0.imprint","INTERSECT",VERTEX,{"derivedFrom":[subQ0,sQuery(id+"F0.wireOp",EDGE,"E47")]}),-1.0]])],"derivedFrom":subQ0})])]}),makeQuery(id+"F7.opExtrude","SWEPT_FACE",FACE,{"disambiguationData":[OSD([subQ0]),TDD([makeQuery(id+"F0.imprint","IMPRINT",EDGE,{"disambiguationData":[TD([[makeQuery(id+"F0.imprint","INTERSECT",VERTEX,{"derivedFrom":[subQ0,sQuery(id+"F0.wireOp",EDGE,"E75")]}),-1.0]])],"derivedFrom":subQ0}),makeQuery(id+"F0.imprint","IMPRINT",EDGE,{"disambiguationData":[TD([[subQ2,-1.0]])],"derivedFrom":subQ0})])]}),makeQuery(id+"F7.opExtrude","SWEPT_FACE",FACE,{"disambiguationData":[OSD([subQ0]),TDD([makeQuery(id+"F0.imprint","IMPRINT",EDGE,{"disambiguationData":[TD([[makeQuery(id+"F0.imprint","INTERSECT",VERTEX,{"derivedFrom":[subQ0,sQuery(id+"F0.wireOp",EDGE,"E81")]}),-1.0]])],"derivedFrom":subQ0})])]}),makeQuery(id+"F7.opExtrude","SWEPT_FACE",FACE,{"disambiguationData":[OSD([subQ0]),TDD([makeQuery(id+"F0.imprint","IMPRINT",EDGE,{"disambiguationData":[TD([[makeQuery(id+"F0.imprint","INTERSECT",VERTEX,{"derivedFrom":[subQ0,sQuery(id+"F0.wireOp",EDGE,"E13")]}),1.0]])],"derivedFrom":subQ0})])]}),makeQuery(id+"F7.opExtrude","SWEPT_FACE",FACE,{"disambiguationData":[OSD([subQ0]),TDD([makeQuery(id+"F0.imprint","IMPRINT",EDGE,{"disambiguationData":[TD([[makeQuery(id+"F0.imprint","INTERSECT",VERTEX,{"derivedFrom":[subQ0,sQuery(id+"F0.wireOp",EDGE,"E9")]}),-1.0]])],"derivedFrom":subQ0})])]}),makeQuery(id+"F7.opExtrude","SWEPT_FACE",FACE,{"disambiguationData":[OSD([subQ0]),TDD([makeQuery(id+"F0.imprint","IMPRINT",EDGE,{"disambiguationData":[TD([[makeQuery(id+"F0.imprint","INTERSECT",VERTEX,{"derivedFrom":[subQ0,sQuery(id+"F0.wireOp",EDGE,"E52")]}),1.0]])],"derivedFrom":subQ0})])]}),makeQuery(id+"F7.opExtrude","SWEPT_FACE",FACE,{"disambiguationData":[OSD([subQ0]),TDD([makeQuery(id+"F0.imprint","IMPRINT",EDGE,{"disambiguationData":[TD([[makeQuery(id+"F0.imprint","INTERSECT",VERTEX,{"derivedFrom":[subQ0,sQuery(id+"F0.wireOp",EDGE,"E50")]}),-1.0]])],"derivedFrom":subQ0})])]}),makeQuery(id+"F7.opExtrude","SWEPT_FACE",FACE,{"disambiguationData":[OSD([subQ0]),TDD([makeQuery(id+"F0.imprint","IMPRINT",EDGE,{"disambiguationData":[TD([[makeQuery(id+"F0.imprint","INTERSECT",VERTEX,{"derivedFrom":[subQ0,sQuery(id+"F0.wireOp",EDGE,"E31")]}),1.0]])],"derivedFrom":subQ0})])]}),makeQuery(id+"F7.opExtrude","SWEPT_FACE",FACE,{"disambiguationData":[OSD([subQ0]),TDD([subQ1])]})]})]});}
            var Q20;
            {var subQ0=sQuery(id+"F0.wireOp",EDGE,"E0");var subQ1=makeQuery(id+"F0.imprint","IMPRINT",EDGE,{"disambiguationData":[TD([[makeQuery(id+"F0.imprint","INTERSECT",VERTEX,{"derivedFrom":[subQ0,sQuery(id+"F0.wireOp",EDGE,"E33")]}),-1.0]])],"derivedFrom":subQ0});var subQ2=makeQuery(id+"F0.imprint","INTERSECT",VERTEX,{"derivedFrom":[subQ0,sQuery(id+"F0.wireOp",EDGE,"E69")]});Q20=makeQuery(id+"F8.opChamfer","BLEND_EDGE",EDGE,{"disambiguationData":[OD(0.0)],"blendedFrom":[makeQuery(id+"F7.opExtrude","CAP_EDGE",EDGE,{"disambiguationData":[OSD([subQ0]),TDD([subQ1])],"isStart":false}),makeQuery(id+"F7.boolean.opBoolean","MERGE",FACE,{"derivedFrom":[makeQuery(id+"F6.opExtrude","SWEPT_FACE",FACE,{"disambiguationData":[OSD([sQuery(id+"F1.wireOp",EDGE,"E89")])]}),makeQuery(id+"F7.opExtrude","SWEPT_FACE",FACE,{"disambiguationData":[OSD([subQ0]),TDD([makeQuery(id+"F0.imprint","IMPRINT",EDGE,{"disambiguationData":[TD([[makeQuery(id+"F0.imprint","INTERSECT",VERTEX,{"derivedFrom":[subQ0,sQuery(id+"F0.wireOp",EDGE,"E47")]}),-1.0]])],"derivedFrom":subQ0})])]}),makeQuery(id+"F7.opExtrude","SWEPT_FACE",FACE,{"disambiguationData":[OSD([subQ0]),TDD([makeQuery(id+"F0.imprint","IMPRINT",EDGE,{"disambiguationData":[TD([[makeQuery(id+"F0.imprint","INTERSECT",VERTEX,{"derivedFrom":[subQ0,sQuery(id+"F0.wireOp",EDGE,"E75")]}),-1.0]])],"derivedFrom":subQ0}),makeQuery(id+"F0.imprint","IMPRINT",EDGE,{"disambiguationData":[TD([[subQ2,-1.0]])],"derivedFrom":subQ0})])]}),makeQuery(id+"F7.opExtrude","SWEPT_FACE",FACE,{"disambiguationData":[OSD([subQ0]),TDD([makeQuery(id+"F0.imprint","IMPRINT",EDGE,{"disambiguationData":[TD([[makeQuery(id+"F0.imprint","INTERSECT",VERTEX,{"derivedFrom":[subQ0,sQuery(id+"F0.wireOp",EDGE,"E81")]}),-1.0]])],"derivedFrom":subQ0})])]}),makeQuery(id+"F7.opExtrude","SWEPT_FACE",FACE,{"disambiguationData":[OSD([subQ0]),TDD([makeQuery(id+"F0.imprint","IMPRINT",EDGE,{"disambiguationData":[TD([[makeQuery(id+"F0.imprint","INTERSECT",VERTEX,{"derivedFrom":[subQ0,sQuery(id+"F0.wireOp",EDGE,"E13")]}),1.0]])],"derivedFrom":subQ0})])]}),makeQuery(id+"F7.opExtrude","SWEPT_FACE",FACE,{"disambiguationData":[OSD([subQ0]),TDD([makeQuery(id+"F0.imprint","IMPRINT",EDGE,{"disambiguationData":[TD([[makeQuery(id+"F0.imprint","INTERSECT",VERTEX,{"derivedFrom":[subQ0,sQuery(id+"F0.wireOp",EDGE,"E9")]}),-1.0]])],"derivedFrom":subQ0})])]}),makeQuery(id+"F7.opExtrude","SWEPT_FACE",FACE,{"disambiguationData":[OSD([subQ0]),TDD([makeQuery(id+"F0.imprint","IMPRINT",EDGE,{"disambiguationData":[TD([[makeQuery(id+"F0.imprint","INTERSECT",VERTEX,{"derivedFrom":[subQ0,sQuery(id+"F0.wireOp",EDGE,"E52")]}),1.0]])],"derivedFrom":subQ0})])]}),makeQuery(id+"F7.opExtrude","SWEPT_FACE",FACE,{"disambiguationData":[OSD([subQ0]),TDD([makeQuery(id+"F0.imprint","IMPRINT",EDGE,{"disambiguationData":[TD([[makeQuery(id+"F0.imprint","INTERSECT",VERTEX,{"derivedFrom":[subQ0,sQuery(id+"F0.wireOp",EDGE,"E50")]}),-1.0]])],"derivedFrom":subQ0})])]}),makeQuery(id+"F7.opExtrude","SWEPT_FACE",FACE,{"disambiguationData":[OSD([subQ0]),TDD([makeQuery(id+"F0.imprint","IMPRINT",EDGE,{"disambiguationData":[TD([[makeQuery(id+"F0.imprint","INTERSECT",VERTEX,{"derivedFrom":[subQ0,sQuery(id+"F0.wireOp",EDGE,"E31")]}),1.0]])],"derivedFrom":subQ0})])]}),makeQuery(id+"F7.opExtrude","SWEPT_FACE",FACE,{"disambiguationData":[OSD([subQ0]),TDD([subQ1])]})]})],"blendedInto":[makeQuery(id+"F7.boolean.opBoolean","MERGE",FACE,{"derivedFrom":[makeQuery(id+"F6.opExtrude","SWEPT_FACE",FACE,{"disambiguationData":[OSD([sQuery(id+"F1.wireOp",EDGE,"E89")])]}),makeQuery(id+"F7.opExtrude","SWEPT_FACE",FACE,{"disambiguationData":[OSD([subQ0]),TDD([makeQuery(id+"F0.imprint","IMPRINT",EDGE,{"disambiguationData":[TD([[makeQuery(id+"F0.imprint","INTERSECT",VERTEX,{"derivedFrom":[subQ0,sQuery(id+"F0.wireOp",EDGE,"E47")]}),-1.0]])],"derivedFrom":subQ0})])]}),makeQuery(id+"F7.opExtrude","SWEPT_FACE",FACE,{"disambiguationData":[OSD([subQ0]),TDD([makeQuery(id+"F0.imprint","IMPRINT",EDGE,{"disambiguationData":[TD([[makeQuery(id+"F0.imprint","INTERSECT",VERTEX,{"derivedFrom":[subQ0,sQuery(id+"F0.wireOp",EDGE,"E75")]}),-1.0]])],"derivedFrom":subQ0}),makeQuery(id+"F0.imprint","IMPRINT",EDGE,{"disambiguationData":[TD([[subQ2,-1.0]])],"derivedFrom":subQ0})])]}),makeQuery(id+"F7.opExtrude","SWEPT_FACE",FACE,{"disambiguationData":[OSD([subQ0]),TDD([makeQuery(id+"F0.imprint","IMPRINT",EDGE,{"disambiguationData":[TD([[makeQuery(id+"F0.imprint","INTERSECT",VERTEX,{"derivedFrom":[subQ0,sQuery(id+"F0.wireOp",EDGE,"E81")]}),-1.0]])],"derivedFrom":subQ0})])]}),makeQuery(id+"F7.opExtrude","SWEPT_FACE",FACE,{"disambiguationData":[OSD([subQ0]),TDD([makeQuery(id+"F0.imprint","IMPRINT",EDGE,{"disambiguationData":[TD([[makeQuery(id+"F0.imprint","INTERSECT",VERTEX,{"derivedFrom":[subQ0,sQuery(id+"F0.wireOp",EDGE,"E13")]}),1.0]])],"derivedFrom":subQ0})])]}),makeQuery(id+"F7.opExtrude","SWEPT_FACE",FACE,{"disambiguationData":[OSD([subQ0]),TDD([makeQuery(id+"F0.imprint","IMPRINT",EDGE,{"disambiguationData":[TD([[makeQuery(id+"F0.imprint","INTERSECT",VERTEX,{"derivedFrom":[subQ0,sQuery(id+"F0.wireOp",EDGE,"E9")]}),-1.0]])],"derivedFrom":subQ0})])]}),makeQuery(id+"F7.opExtrude","SWEPT_FACE",FACE,{"disambiguationData":[OSD([subQ0]),TDD([makeQuery(id+"F0.imprint","IMPRINT",EDGE,{"disambiguationData":[TD([[makeQuery(id+"F0.imprint","INTERSECT",VERTEX,{"derivedFrom":[subQ0,sQuery(id+"F0.wireOp",EDGE,"E52")]}),1.0]])],"derivedFrom":subQ0})])]}),makeQuery(id+"F7.opExtrude","SWEPT_FACE",FACE,{"disambiguationData":[OSD([subQ0]),TDD([makeQuery(id+"F0.imprint","IMPRINT",EDGE,{"disambiguationData":[TD([[makeQuery(id+"F0.imprint","INTERSECT",VERTEX,{"derivedFrom":[subQ0,sQuery(id+"F0.wireOp",EDGE,"E50")]}),-1.0]])],"derivedFrom":subQ0})])]}),makeQuery(id+"F7.opExtrude","SWEPT_FACE",FACE,{"disambiguationData":[OSD([subQ0]),TDD([makeQuery(id+"F0.imprint","IMPRINT",EDGE,{"disambiguationData":[TD([[makeQuery(id+"F0.imprint","INTERSECT",VERTEX,{"derivedFrom":[subQ0,sQuery(id+"F0.wireOp",EDGE,"E31")]}),1.0]])],"derivedFrom":subQ0})])]}),makeQuery(id+"F7.opExtrude","SWEPT_FACE",FACE,{"disambiguationData":[OSD([subQ0]),TDD([subQ1])]})]})]});}
            var Q21;
            {var subQ0=sQuery(id+"F0.wireOp",EDGE,"E0");var subQ1=makeQuery(id+"F0.imprint","IMPRINT",EDGE,{"disambiguationData":[TD([[makeQuery(id+"F0.imprint","INTERSECT",VERTEX,{"derivedFrom":[subQ0,sQuery(id+"F0.wireOp",EDGE,"E13")]}),1.0]])],"derivedFrom":subQ0});var subQ2=makeQuery(id+"F0.imprint","INTERSECT",VERTEX,{"derivedFrom":[subQ0,sQuery(id+"F0.wireOp",EDGE,"E69")]});Q21=makeQuery(id+"F8.opChamfer","BLEND_EDGE",EDGE,{"disambiguationData":[OD(2.0)],"blendedFrom":[makeQuery(id+"F7.opExtrude","CAP_EDGE",EDGE,{"disambiguationData":[OSD([subQ0]),TDD([subQ1])],"isStart":false}),makeQuery(id+"F7.boolean.opBoolean","MERGE",FACE,{"derivedFrom":[makeQuery(id+"F6.opExtrude","SWEPT_FACE",FACE,{"disambiguationData":[OSD([sQuery(id+"F1.wireOp",EDGE,"E89")])]}),makeQuery(id+"F7.opExtrude","SWEPT_FACE",FACE,{"disambiguationData":[OSD([subQ0]),TDD([makeQuery(id+"F0.imprint","IMPRINT",EDGE,{"disambiguationData":[TD([[makeQuery(id+"F0.imprint","INTERSECT",VERTEX,{"derivedFrom":[subQ0,sQuery(id+"F0.wireOp",EDGE,"E47")]}),-1.0]])],"derivedFrom":subQ0})])]}),makeQuery(id+"F7.opExtrude","SWEPT_FACE",FACE,{"disambiguationData":[OSD([subQ0]),TDD([makeQuery(id+"F0.imprint","IMPRINT",EDGE,{"disambiguationData":[TD([[makeQuery(id+"F0.imprint","INTERSECT",VERTEX,{"derivedFrom":[subQ0,sQuery(id+"F0.wireOp",EDGE,"E75")]}),-1.0]])],"derivedFrom":subQ0}),makeQuery(id+"F0.imprint","IMPRINT",EDGE,{"disambiguationData":[TD([[subQ2,-1.0]])],"derivedFrom":subQ0})])]}),makeQuery(id+"F7.opExtrude","SWEPT_FACE",FACE,{"disambiguationData":[OSD([subQ0]),TDD([makeQuery(id+"F0.imprint","IMPRINT",EDGE,{"disambiguationData":[TD([[makeQuery(id+"F0.imprint","INTERSECT",VERTEX,{"derivedFrom":[subQ0,sQuery(id+"F0.wireOp",EDGE,"E81")]}),-1.0]])],"derivedFrom":subQ0})])]}),makeQuery(id+"F7.opExtrude","SWEPT_FACE",FACE,{"disambiguationData":[OSD([subQ0]),TDD([subQ1])]}),makeQuery(id+"F7.opExtrude","SWEPT_FACE",FACE,{"disambiguationData":[OSD([subQ0]),TDD([makeQuery(id+"F0.imprint","IMPRINT",EDGE,{"disambiguationData":[TD([[makeQuery(id+"F0.imprint","INTERSECT",VERTEX,{"derivedFrom":[subQ0,sQuery(id+"F0.wireOp",EDGE,"E9")]}),-1.0]])],"derivedFrom":subQ0})])]}),makeQuery(id+"F7.opExtrude","SWEPT_FACE",FACE,{"disambiguationData":[OSD([subQ0]),TDD([makeQuery(id+"F0.imprint","IMPRINT",EDGE,{"disambiguationData":[TD([[makeQuery(id+"F0.imprint","INTERSECT",VERTEX,{"derivedFrom":[subQ0,sQuery(id+"F0.wireOp",EDGE,"E52")]}),1.0]])],"derivedFrom":subQ0})])]}),makeQuery(id+"F7.opExtrude","SWEPT_FACE",FACE,{"disambiguationData":[OSD([subQ0]),TDD([makeQuery(id+"F0.imprint","IMPRINT",EDGE,{"disambiguationData":[TD([[makeQuery(id+"F0.imprint","INTERSECT",VERTEX,{"derivedFrom":[subQ0,sQuery(id+"F0.wireOp",EDGE,"E50")]}),-1.0]])],"derivedFrom":subQ0})])]}),makeQuery(id+"F7.opExtrude","SWEPT_FACE",FACE,{"disambiguationData":[OSD([subQ0]),TDD([makeQuery(id+"F0.imprint","IMPRINT",EDGE,{"disambiguationData":[TD([[makeQuery(id+"F0.imprint","INTERSECT",VERTEX,{"derivedFrom":[subQ0,sQuery(id+"F0.wireOp",EDGE,"E31")]}),1.0]])],"derivedFrom":subQ0})])]}),makeQuery(id+"F7.opExtrude","SWEPT_FACE",FACE,{"disambiguationData":[OSD([subQ0]),TDD([makeQuery(id+"F0.imprint","IMPRINT",EDGE,{"disambiguationData":[TD([[makeQuery(id+"F0.imprint","INTERSECT",VERTEX,{"derivedFrom":[subQ0,sQuery(id+"F0.wireOp",EDGE,"E33")]}),-1.0]])],"derivedFrom":subQ0})])]})]})],"blendedInto":[makeQuery(id+"F7.boolean.opBoolean","MERGE",FACE,{"derivedFrom":[makeQuery(id+"F6.opExtrude","SWEPT_FACE",FACE,{"disambiguationData":[OSD([sQuery(id+"F1.wireOp",EDGE,"E89")])]}),makeQuery(id+"F7.opExtrude","SWEPT_FACE",FACE,{"disambiguationData":[OSD([subQ0]),TDD([makeQuery(id+"F0.imprint","IMPRINT",EDGE,{"disambiguationData":[TD([[makeQuery(id+"F0.imprint","INTERSECT",VERTEX,{"derivedFrom":[subQ0,sQuery(id+"F0.wireOp",EDGE,"E47")]}),-1.0]])],"derivedFrom":subQ0})])]}),makeQuery(id+"F7.opExtrude","SWEPT_FACE",FACE,{"disambiguationData":[OSD([subQ0]),TDD([makeQuery(id+"F0.imprint","IMPRINT",EDGE,{"disambiguationData":[TD([[makeQuery(id+"F0.imprint","INTERSECT",VERTEX,{"derivedFrom":[subQ0,sQuery(id+"F0.wireOp",EDGE,"E75")]}),-1.0]])],"derivedFrom":subQ0}),makeQuery(id+"F0.imprint","IMPRINT",EDGE,{"disambiguationData":[TD([[subQ2,-1.0]])],"derivedFrom":subQ0})])]}),makeQuery(id+"F7.opExtrude","SWEPT_FACE",FACE,{"disambiguationData":[OSD([subQ0]),TDD([makeQuery(id+"F0.imprint","IMPRINT",EDGE,{"disambiguationData":[TD([[makeQuery(id+"F0.imprint","INTERSECT",VERTEX,{"derivedFrom":[subQ0,sQuery(id+"F0.wireOp",EDGE,"E81")]}),-1.0]])],"derivedFrom":subQ0})])]}),makeQuery(id+"F7.opExtrude","SWEPT_FACE",FACE,{"disambiguationData":[OSD([subQ0]),TDD([subQ1])]}),makeQuery(id+"F7.opExtrude","SWEPT_FACE",FACE,{"disambiguationData":[OSD([subQ0]),TDD([makeQuery(id+"F0.imprint","IMPRINT",EDGE,{"disambiguationData":[TD([[makeQuery(id+"F0.imprint","INTERSECT",VERTEX,{"derivedFrom":[subQ0,sQuery(id+"F0.wireOp",EDGE,"E9")]}),-1.0]])],"derivedFrom":subQ0})])]}),makeQuery(id+"F7.opExtrude","SWEPT_FACE",FACE,{"disambiguationData":[OSD([subQ0]),TDD([makeQuery(id+"F0.imprint","IMPRINT",EDGE,{"disambiguationData":[TD([[makeQuery(id+"F0.imprint","INTERSECT",VERTEX,{"derivedFrom":[subQ0,sQuery(id+"F0.wireOp",EDGE,"E52")]}),1.0]])],"derivedFrom":subQ0})])]}),makeQuery(id+"F7.opExtrude","SWEPT_FACE",FACE,{"disambiguationData":[OSD([subQ0]),TDD([makeQuery(id+"F0.imprint","IMPRINT",EDGE,{"disambiguationData":[TD([[makeQuery(id+"F0.imprint","INTERSECT",VERTEX,{"derivedFrom":[subQ0,sQuery(id+"F0.wireOp",EDGE,"E50")]}),-1.0]])],"derivedFrom":subQ0})])]}),makeQuery(id+"F7.opExtrude","SWEPT_FACE",FACE,{"disambiguationData":[OSD([subQ0]),TDD([makeQuery(id+"F0.imprint","IMPRINT",EDGE,{"disambiguationData":[TD([[makeQuery(id+"F0.imprint","INTERSECT",VERTEX,{"derivedFrom":[subQ0,sQuery(id+"F0.wireOp",EDGE,"E31")]}),1.0]])],"derivedFrom":subQ0})])]}),makeQuery(id+"F7.opExtrude","SWEPT_FACE",FACE,{"disambiguationData":[OSD([subQ0]),TDD([makeQuery(id+"F0.imprint","IMPRINT",EDGE,{"disambiguationData":[TD([[makeQuery(id+"F0.imprint","INTERSECT",VERTEX,{"derivedFrom":[subQ0,sQuery(id+"F0.wireOp",EDGE,"E33")]}),-1.0]])],"derivedFrom":subQ0})])]})]})]});}
            var Q22;
            {var subQ0=sQuery(id+"F0.wireOp",EDGE,"E0");Q22=makeQuery(id+"F8.opChamfer","BLEND_EDGE",EDGE,{"blendedFrom":[makeQuery(id+"F7.opExtrude","CAP_EDGE",EDGE,{"disambiguationData":[OSD([subQ0]),TDD([makeQuery(id+"F0.imprint","IMPRINT",EDGE,{"disambiguationData":[TD([[makeQuery(id+"F0.imprint","INTERSECT",VERTEX,{"derivedFrom":[subQ0,sQuery(id+"F0.wireOp",EDGE,"E13")]}),1.0]])],"derivedFrom":subQ0})])],"isStart":false}),makeQuery(id+"F7.opExtrude","SWEPT_FACE",FACE,{"disambiguationData":[OSD([sQuery(id+"F0.wireOp",EDGE,"E11")])]})],"blendedInto":[makeQuery(id+"F7.opExtrude","SWEPT_FACE",FACE,{"disambiguationData":[OSD([sQuery(id+"F0.wireOp",EDGE,"E11")])]})]});}
            var Q23;
            {var subQ0=sQuery(id+"F0.wireOp",EDGE,"E12");var subQ1=sQuery(id+"F0.wireOp",EDGE,"E0");Q23=makeQuery(id+"F8.opChamfer","BLEND_EDGE",EDGE,{"blendedFrom":[makeQuery(id+"F7.opExtrude","CAP_EDGE",EDGE,{"disambiguationData":[OSD([subQ1]),TDD([makeQuery(id+"F0.imprint","IMPRINT",EDGE,{"disambiguationData":[TD([[makeQuery(id+"F0.imprint","INTERSECT",VERTEX,{"derivedFrom":[subQ1,sQuery(id+"F0.wireOp",EDGE,"E13")]}),1.0]])],"derivedFrom":subQ1})])],"isStart":false}),makeQuery(id+"F7.opExtrude","SWEPT_FACE",FACE,{"disambiguationData":[OSD([subQ0]),TDD([makeQuery(id+"F0.imprint","IMPRINT",EDGE,{"disambiguationData":[TD([[makeQuery(id+"F0.imprint","INTERSECT",VERTEX,{"derivedFrom":[subQ0,sQuery(id+"F0.wireOp",EDGE,"E18.1")]}),-1.0]])],"derivedFrom":subQ0})])]})],"blendedInto":[makeQuery(id+"F7.opExtrude","SWEPT_FACE",FACE,{"disambiguationData":[OSD([subQ0]),TDD([makeQuery(id+"F0.imprint","IMPRINT",EDGE,{"disambiguationData":[TD([[makeQuery(id+"F0.imprint","INTERSECT",VERTEX,{"derivedFrom":[subQ0,sQuery(id+"F0.wireOp",EDGE,"E18.1")]}),-1.0]])],"derivedFrom":subQ0})])]})]});}
            var Q24;
            {var subQ0=sQuery(id+"F0.wireOp",EDGE,"E13");var subQ1=sQuery(id+"F0.wireOp",EDGE,"E12");var subQ2=sQuery(id+"F0.wireOp",EDGE,"E0");Q24=makeQuery(id+"F8.opChamfer","BLEND_EDGE",EDGE,{"blendedFrom":[makeQuery(id+"F7.opExtrude","CAP_EDGE",EDGE,{"disambiguationData":[OSD([subQ2]),TDD([makeQuery(id+"F0.imprint","IMPRINT",EDGE,{"disambiguationData":[TD([[makeQuery(id+"F0.imprint","INTERSECT",VERTEX,{"derivedFrom":[subQ2,subQ0]}),1.0]])],"derivedFrom":subQ2})])],"isStart":false}),makeQuery(id+"F7.opExtrude","SWEPT_FACE",FACE,{"disambiguationData":[OSD([subQ1]),TDD([makeQuery(id+"F0.imprint","IMPRINT",EDGE,{"disambiguationData":[TD([[makeQuery(id+"F0.imprint","INTERSECT",VERTEX,{"derivedFrom":[subQ1,subQ0]}),-1.0]])],"derivedFrom":subQ1})])]})],"blendedInto":[makeQuery(id+"F7.opExtrude","SWEPT_FACE",FACE,{"disambiguationData":[OSD([subQ1]),TDD([makeQuery(id+"F0.imprint","IMPRINT",EDGE,{"disambiguationData":[TD([[makeQuery(id+"F0.imprint","INTERSECT",VERTEX,{"derivedFrom":[subQ1,subQ0]}),-1.0]])],"derivedFrom":subQ1})])]})]});}
            var Q25;
            {var subQ0=sQuery(id+"F0.wireOp",EDGE,"E0");var subQ1=makeQuery(id+"F0.imprint","IMPRINT",EDGE,{"disambiguationData":[TD([[makeQuery(id+"F0.imprint","INTERSECT",VERTEX,{"derivedFrom":[subQ0,sQuery(id+"F0.wireOp",EDGE,"E13")]}),1.0]])],"derivedFrom":subQ0});var subQ2=makeQuery(id+"F0.imprint","INTERSECT",VERTEX,{"derivedFrom":[subQ0,sQuery(id+"F0.wireOp",EDGE,"E69")]});Q25=makeQuery(id+"F8.opChamfer","BLEND_EDGE",EDGE,{"disambiguationData":[OD(1.0)],"blendedFrom":[makeQuery(id+"F7.opExtrude","CAP_EDGE",EDGE,{"disambiguationData":[OSD([subQ0]),TDD([subQ1])],"isStart":false}),makeQuery(id+"F7.boolean.opBoolean","MERGE",FACE,{"derivedFrom":[makeQuery(id+"F6.opExtrude","SWEPT_FACE",FACE,{"disambiguationData":[OSD([sQuery(id+"F1.wireOp",EDGE,"E89")])]}),makeQuery(id+"F7.opExtrude","SWEPT_FACE",FACE,{"disambiguationData":[OSD([subQ0]),TDD([makeQuery(id+"F0.imprint","IMPRINT",EDGE,{"disambiguationData":[TD([[makeQuery(id+"F0.imprint","INTERSECT",VERTEX,{"derivedFrom":[subQ0,sQuery(id+"F0.wireOp",EDGE,"E47")]}),-1.0]])],"derivedFrom":subQ0})])]}),makeQuery(id+"F7.opExtrude","SWEPT_FACE",FACE,{"disambiguationData":[OSD([subQ0]),TDD([makeQuery(id+"F0.imprint","IMPRINT",EDGE,{"disambiguationData":[TD([[makeQuery(id+"F0.imprint","INTERSECT",VERTEX,{"derivedFrom":[subQ0,sQuery(id+"F0.wireOp",EDGE,"E75")]}),-1.0]])],"derivedFrom":subQ0}),makeQuery(id+"F0.imprint","IMPRINT",EDGE,{"disambiguationData":[TD([[subQ2,-1.0]])],"derivedFrom":subQ0})])]}),makeQuery(id+"F7.opExtrude","SWEPT_FACE",FACE,{"disambiguationData":[OSD([subQ0]),TDD([makeQuery(id+"F0.imprint","IMPRINT",EDGE,{"disambiguationData":[TD([[makeQuery(id+"F0.imprint","INTERSECT",VERTEX,{"derivedFrom":[subQ0,sQuery(id+"F0.wireOp",EDGE,"E81")]}),-1.0]])],"derivedFrom":subQ0})])]}),makeQuery(id+"F7.opExtrude","SWEPT_FACE",FACE,{"disambiguationData":[OSD([subQ0]),TDD([subQ1])]}),makeQuery(id+"F7.opExtrude","SWEPT_FACE",FACE,{"disambiguationData":[OSD([subQ0]),TDD([makeQuery(id+"F0.imprint","IMPRINT",EDGE,{"disambiguationData":[TD([[makeQuery(id+"F0.imprint","INTERSECT",VERTEX,{"derivedFrom":[subQ0,sQuery(id+"F0.wireOp",EDGE,"E9")]}),-1.0]])],"derivedFrom":subQ0})])]}),makeQuery(id+"F7.opExtrude","SWEPT_FACE",FACE,{"disambiguationData":[OSD([subQ0]),TDD([makeQuery(id+"F0.imprint","IMPRINT",EDGE,{"disambiguationData":[TD([[makeQuery(id+"F0.imprint","INTERSECT",VERTEX,{"derivedFrom":[subQ0,sQuery(id+"F0.wireOp",EDGE,"E52")]}),1.0]])],"derivedFrom":subQ0})])]}),makeQuery(id+"F7.opExtrude","SWEPT_FACE",FACE,{"disambiguationData":[OSD([subQ0]),TDD([makeQuery(id+"F0.imprint","IMPRINT",EDGE,{"disambiguationData":[TD([[makeQuery(id+"F0.imprint","INTERSECT",VERTEX,{"derivedFrom":[subQ0,sQuery(id+"F0.wireOp",EDGE,"E50")]}),-1.0]])],"derivedFrom":subQ0})])]}),makeQuery(id+"F7.opExtrude","SWEPT_FACE",FACE,{"disambiguationData":[OSD([subQ0]),TDD([makeQuery(id+"F0.imprint","IMPRINT",EDGE,{"disambiguationData":[TD([[makeQuery(id+"F0.imprint","INTERSECT",VERTEX,{"derivedFrom":[subQ0,sQuery(id+"F0.wireOp",EDGE,"E31")]}),1.0]])],"derivedFrom":subQ0})])]}),makeQuery(id+"F7.opExtrude","SWEPT_FACE",FACE,{"disambiguationData":[OSD([subQ0]),TDD([makeQuery(id+"F0.imprint","IMPRINT",EDGE,{"disambiguationData":[TD([[makeQuery(id+"F0.imprint","INTERSECT",VERTEX,{"derivedFrom":[subQ0,sQuery(id+"F0.wireOp",EDGE,"E33")]}),-1.0]])],"derivedFrom":subQ0})])]})]})],"blendedInto":[makeQuery(id+"F7.boolean.opBoolean","MERGE",FACE,{"derivedFrom":[makeQuery(id+"F6.opExtrude","SWEPT_FACE",FACE,{"disambiguationData":[OSD([sQuery(id+"F1.wireOp",EDGE,"E89")])]}),makeQuery(id+"F7.opExtrude","SWEPT_FACE",FACE,{"disambiguationData":[OSD([subQ0]),TDD([makeQuery(id+"F0.imprint","IMPRINT",EDGE,{"disambiguationData":[TD([[makeQuery(id+"F0.imprint","INTERSECT",VERTEX,{"derivedFrom":[subQ0,sQuery(id+"F0.wireOp",EDGE,"E47")]}),-1.0]])],"derivedFrom":subQ0})])]}),makeQuery(id+"F7.opExtrude","SWEPT_FACE",FACE,{"disambiguationData":[OSD([subQ0]),TDD([makeQuery(id+"F0.imprint","IMPRINT",EDGE,{"disambiguationData":[TD([[makeQuery(id+"F0.imprint","INTERSECT",VERTEX,{"derivedFrom":[subQ0,sQuery(id+"F0.wireOp",EDGE,"E75")]}),-1.0]])],"derivedFrom":subQ0}),makeQuery(id+"F0.imprint","IMPRINT",EDGE,{"disambiguationData":[TD([[subQ2,-1.0]])],"derivedFrom":subQ0})])]}),makeQuery(id+"F7.opExtrude","SWEPT_FACE",FACE,{"disambiguationData":[OSD([subQ0]),TDD([makeQuery(id+"F0.imprint","IMPRINT",EDGE,{"disambiguationData":[TD([[makeQuery(id+"F0.imprint","INTERSECT",VERTEX,{"derivedFrom":[subQ0,sQuery(id+"F0.wireOp",EDGE,"E81")]}),-1.0]])],"derivedFrom":subQ0})])]}),makeQuery(id+"F7.opExtrude","SWEPT_FACE",FACE,{"disambiguationData":[OSD([subQ0]),TDD([subQ1])]}),makeQuery(id+"F7.opExtrude","SWEPT_FACE",FACE,{"disambiguationData":[OSD([subQ0]),TDD([makeQuery(id+"F0.imprint","IMPRINT",EDGE,{"disambiguationData":[TD([[makeQuery(id+"F0.imprint","INTERSECT",VERTEX,{"derivedFrom":[subQ0,sQuery(id+"F0.wireOp",EDGE,"E9")]}),-1.0]])],"derivedFrom":subQ0})])]}),makeQuery(id+"F7.opExtrude","SWEPT_FACE",FACE,{"disambiguationData":[OSD([subQ0]),TDD([makeQuery(id+"F0.imprint","IMPRINT",EDGE,{"disambiguationData":[TD([[makeQuery(id+"F0.imprint","INTERSECT",VERTEX,{"derivedFrom":[subQ0,sQuery(id+"F0.wireOp",EDGE,"E52")]}),1.0]])],"derivedFrom":subQ0})])]}),makeQuery(id+"F7.opExtrude","SWEPT_FACE",FACE,{"disambiguationData":[OSD([subQ0]),TDD([makeQuery(id+"F0.imprint","IMPRINT",EDGE,{"disambiguationData":[TD([[makeQuery(id+"F0.imprint","INTERSECT",VERTEX,{"derivedFrom":[subQ0,sQuery(id+"F0.wireOp",EDGE,"E50")]}),-1.0]])],"derivedFrom":subQ0})])]}),makeQuery(id+"F7.opExtrude","SWEPT_FACE",FACE,{"disambiguationData":[OSD([subQ0]),TDD([makeQuery(id+"F0.imprint","IMPRINT",EDGE,{"disambiguationData":[TD([[makeQuery(id+"F0.imprint","INTERSECT",VERTEX,{"derivedFrom":[subQ0,sQuery(id+"F0.wireOp",EDGE,"E31")]}),1.0]])],"derivedFrom":subQ0})])]}),makeQuery(id+"F7.opExtrude","SWEPT_FACE",FACE,{"disambiguationData":[OSD([subQ0]),TDD([makeQuery(id+"F0.imprint","IMPRINT",EDGE,{"disambiguationData":[TD([[makeQuery(id+"F0.imprint","INTERSECT",VERTEX,{"derivedFrom":[subQ0,sQuery(id+"F0.wireOp",EDGE,"E33")]}),-1.0]])],"derivedFrom":subQ0})])]})]})]});}
            var Q26;
            {var subQ0=sQuery(id+"F0.wireOp",EDGE,"E0");var subQ1=makeQuery(id+"F0.imprint","IMPRINT",EDGE,{"disambiguationData":[TD([[makeQuery(id+"F0.imprint","INTERSECT",VERTEX,{"derivedFrom":[subQ0,sQuery(id+"F0.wireOp",EDGE,"E81")]}),-1.0]])],"derivedFrom":subQ0});var subQ2=makeQuery(id+"F0.imprint","INTERSECT",VERTEX,{"derivedFrom":[subQ0,sQuery(id+"F0.wireOp",EDGE,"E69")]});Q26=makeQuery(id+"F8.opChamfer","BLEND_EDGE",EDGE,{"disambiguationData":[OD(0.0)],"blendedFrom":[makeQuery(id+"F7.opExtrude","CAP_EDGE",EDGE,{"disambiguationData":[OSD([subQ0]),TDD([subQ1])],"isStart":false}),makeQuery(id+"F7.boolean.opBoolean","MERGE",FACE,{"derivedFrom":[makeQuery(id+"F6.opExtrude","SWEPT_FACE",FACE,{"disambiguationData":[OSD([sQuery(id+"F1.wireOp",EDGE,"E89")])]}),makeQuery(id+"F7.opExtrude","SWEPT_FACE",FACE,{"disambiguationData":[OSD([subQ0]),TDD([makeQuery(id+"F0.imprint","IMPRINT",EDGE,{"disambiguationData":[TD([[makeQuery(id+"F0.imprint","INTERSECT",VERTEX,{"derivedFrom":[subQ0,sQuery(id+"F0.wireOp",EDGE,"E47")]}),-1.0]])],"derivedFrom":subQ0})])]}),makeQuery(id+"F7.opExtrude","SWEPT_FACE",FACE,{"disambiguationData":[OSD([subQ0]),TDD([makeQuery(id+"F0.imprint","IMPRINT",EDGE,{"disambiguationData":[TD([[makeQuery(id+"F0.imprint","INTERSECT",VERTEX,{"derivedFrom":[subQ0,sQuery(id+"F0.wireOp",EDGE,"E75")]}),-1.0]])],"derivedFrom":subQ0}),makeQuery(id+"F0.imprint","IMPRINT",EDGE,{"disambiguationData":[TD([[subQ2,-1.0]])],"derivedFrom":subQ0})])]}),makeQuery(id+"F7.opExtrude","SWEPT_FACE",FACE,{"disambiguationData":[OSD([subQ0]),TDD([subQ1])]}),makeQuery(id+"F7.opExtrude","SWEPT_FACE",FACE,{"disambiguationData":[OSD([subQ0]),TDD([makeQuery(id+"F0.imprint","IMPRINT",EDGE,{"disambiguationData":[TD([[makeQuery(id+"F0.imprint","INTERSECT",VERTEX,{"derivedFrom":[subQ0,sQuery(id+"F0.wireOp",EDGE,"E13")]}),1.0]])],"derivedFrom":subQ0})])]}),makeQuery(id+"F7.opExtrude","SWEPT_FACE",FACE,{"disambiguationData":[OSD([subQ0]),TDD([makeQuery(id+"F0.imprint","IMPRINT",EDGE,{"disambiguationData":[TD([[makeQuery(id+"F0.imprint","INTERSECT",VERTEX,{"derivedFrom":[subQ0,sQuery(id+"F0.wireOp",EDGE,"E9")]}),-1.0]])],"derivedFrom":subQ0})])]}),makeQuery(id+"F7.opExtrude","SWEPT_FACE",FACE,{"disambiguationData":[OSD([subQ0]),TDD([makeQuery(id+"F0.imprint","IMPRINT",EDGE,{"disambiguationData":[TD([[makeQuery(id+"F0.imprint","INTERSECT",VERTEX,{"derivedFrom":[subQ0,sQuery(id+"F0.wireOp",EDGE,"E52")]}),1.0]])],"derivedFrom":subQ0})])]}),makeQuery(id+"F7.opExtrude","SWEPT_FACE",FACE,{"disambiguationData":[OSD([subQ0]),TDD([makeQuery(id+"F0.imprint","IMPRINT",EDGE,{"disambiguationData":[TD([[makeQuery(id+"F0.imprint","INTERSECT",VERTEX,{"derivedFrom":[subQ0,sQuery(id+"F0.wireOp",EDGE,"E50")]}),-1.0]])],"derivedFrom":subQ0})])]}),makeQuery(id+"F7.opExtrude","SWEPT_FACE",FACE,{"disambiguationData":[OSD([subQ0]),TDD([makeQuery(id+"F0.imprint","IMPRINT",EDGE,{"disambiguationData":[TD([[makeQuery(id+"F0.imprint","INTERSECT",VERTEX,{"derivedFrom":[subQ0,sQuery(id+"F0.wireOp",EDGE,"E31")]}),1.0]])],"derivedFrom":subQ0})])]}),makeQuery(id+"F7.opExtrude","SWEPT_FACE",FACE,{"disambiguationData":[OSD([subQ0]),TDD([makeQuery(id+"F0.imprint","IMPRINT",EDGE,{"disambiguationData":[TD([[makeQuery(id+"F0.imprint","INTERSECT",VERTEX,{"derivedFrom":[subQ0,sQuery(id+"F0.wireOp",EDGE,"E33")]}),-1.0]])],"derivedFrom":subQ0})])]})]})],"blendedInto":[makeQuery(id+"F7.boolean.opBoolean","MERGE",FACE,{"derivedFrom":[makeQuery(id+"F6.opExtrude","SWEPT_FACE",FACE,{"disambiguationData":[OSD([sQuery(id+"F1.wireOp",EDGE,"E89")])]}),makeQuery(id+"F7.opExtrude","SWEPT_FACE",FACE,{"disambiguationData":[OSD([subQ0]),TDD([makeQuery(id+"F0.imprint","IMPRINT",EDGE,{"disambiguationData":[TD([[makeQuery(id+"F0.imprint","INTERSECT",VERTEX,{"derivedFrom":[subQ0,sQuery(id+"F0.wireOp",EDGE,"E47")]}),-1.0]])],"derivedFrom":subQ0})])]}),makeQuery(id+"F7.opExtrude","SWEPT_FACE",FACE,{"disambiguationData":[OSD([subQ0]),TDD([makeQuery(id+"F0.imprint","IMPRINT",EDGE,{"disambiguationData":[TD([[makeQuery(id+"F0.imprint","INTERSECT",VERTEX,{"derivedFrom":[subQ0,sQuery(id+"F0.wireOp",EDGE,"E75")]}),-1.0]])],"derivedFrom":subQ0}),makeQuery(id+"F0.imprint","IMPRINT",EDGE,{"disambiguationData":[TD([[subQ2,-1.0]])],"derivedFrom":subQ0})])]}),makeQuery(id+"F7.opExtrude","SWEPT_FACE",FACE,{"disambiguationData":[OSD([subQ0]),TDD([subQ1])]}),makeQuery(id+"F7.opExtrude","SWEPT_FACE",FACE,{"disambiguationData":[OSD([subQ0]),TDD([makeQuery(id+"F0.imprint","IMPRINT",EDGE,{"disambiguationData":[TD([[makeQuery(id+"F0.imprint","INTERSECT",VERTEX,{"derivedFrom":[subQ0,sQuery(id+"F0.wireOp",EDGE,"E13")]}),1.0]])],"derivedFrom":subQ0})])]}),makeQuery(id+"F7.opExtrude","SWEPT_FACE",FACE,{"disambiguationData":[OSD([subQ0]),TDD([makeQuery(id+"F0.imprint","IMPRINT",EDGE,{"disambiguationData":[TD([[makeQuery(id+"F0.imprint","INTERSECT",VERTEX,{"derivedFrom":[subQ0,sQuery(id+"F0.wireOp",EDGE,"E9")]}),-1.0]])],"derivedFrom":subQ0})])]}),makeQuery(id+"F7.opExtrude","SWEPT_FACE",FACE,{"disambiguationData":[OSD([subQ0]),TDD([makeQuery(id+"F0.imprint","IMPRINT",EDGE,{"disambiguationData":[TD([[makeQuery(id+"F0.imprint","INTERSECT",VERTEX,{"derivedFrom":[subQ0,sQuery(id+"F0.wireOp",EDGE,"E52")]}),1.0]])],"derivedFrom":subQ0})])]}),makeQuery(id+"F7.opExtrude","SWEPT_FACE",FACE,{"disambiguationData":[OSD([subQ0]),TDD([makeQuery(id+"F0.imprint","IMPRINT",EDGE,{"disambiguationData":[TD([[makeQuery(id+"F0.imprint","INTERSECT",VERTEX,{"derivedFrom":[subQ0,sQuery(id+"F0.wireOp",EDGE,"E50")]}),-1.0]])],"derivedFrom":subQ0})])]}),makeQuery(id+"F7.opExtrude","SWEPT_FACE",FACE,{"disambiguationData":[OSD([subQ0]),TDD([makeQuery(id+"F0.imprint","IMPRINT",EDGE,{"disambiguationData":[TD([[makeQuery(id+"F0.imprint","INTERSECT",VERTEX,{"derivedFrom":[subQ0,sQuery(id+"F0.wireOp",EDGE,"E31")]}),1.0]])],"derivedFrom":subQ0})])]}),makeQuery(id+"F7.opExtrude","SWEPT_FACE",FACE,{"disambiguationData":[OSD([subQ0]),TDD([makeQuery(id+"F0.imprint","IMPRINT",EDGE,{"disambiguationData":[TD([[makeQuery(id+"F0.imprint","INTERSECT",VERTEX,{"derivedFrom":[subQ0,sQuery(id+"F0.wireOp",EDGE,"E33")]}),-1.0]])],"derivedFrom":subQ0})])]})]})]});}
            var Q27;
            {var subQ0=sQuery(id+"F0.wireOp",EDGE,"E0");var subQ1=makeQuery(id+"F0.imprint","IMPRINT",EDGE,{"disambiguationData":[TD([[makeQuery(id+"F0.imprint","INTERSECT",VERTEX,{"derivedFrom":[subQ0,sQuery(id+"F0.wireOp",EDGE,"E81")]}),-1.0]])],"derivedFrom":subQ0});var subQ2=makeQuery(id+"F0.imprint","INTERSECT",VERTEX,{"derivedFrom":[subQ0,sQuery(id+"F0.wireOp",EDGE,"E69")]});Q27=makeQuery(id+"F8.opChamfer","BLEND_EDGE",EDGE,{"disambiguationData":[OD(1.0)],"blendedFrom":[makeQuery(id+"F7.opExtrude","CAP_EDGE",EDGE,{"disambiguationData":[OSD([subQ0]),TDD([subQ1])],"isStart":false}),makeQuery(id+"F7.boolean.opBoolean","MERGE",FACE,{"derivedFrom":[makeQuery(id+"F6.opExtrude","SWEPT_FACE",FACE,{"disambiguationData":[OSD([sQuery(id+"F1.wireOp",EDGE,"E89")])]}),makeQuery(id+"F7.opExtrude","SWEPT_FACE",FACE,{"disambiguationData":[OSD([subQ0]),TDD([makeQuery(id+"F0.imprint","IMPRINT",EDGE,{"disambiguationData":[TD([[makeQuery(id+"F0.imprint","INTERSECT",VERTEX,{"derivedFrom":[subQ0,sQuery(id+"F0.wireOp",EDGE,"E47")]}),-1.0]])],"derivedFrom":subQ0})])]}),makeQuery(id+"F7.opExtrude","SWEPT_FACE",FACE,{"disambiguationData":[OSD([subQ0]),TDD([makeQuery(id+"F0.imprint","IMPRINT",EDGE,{"disambiguationData":[TD([[makeQuery(id+"F0.imprint","INTERSECT",VERTEX,{"derivedFrom":[subQ0,sQuery(id+"F0.wireOp",EDGE,"E75")]}),-1.0]])],"derivedFrom":subQ0}),makeQuery(id+"F0.imprint","IMPRINT",EDGE,{"disambiguationData":[TD([[subQ2,-1.0]])],"derivedFrom":subQ0})])]}),makeQuery(id+"F7.opExtrude","SWEPT_FACE",FACE,{"disambiguationData":[OSD([subQ0]),TDD([subQ1])]}),makeQuery(id+"F7.opExtrude","SWEPT_FACE",FACE,{"disambiguationData":[OSD([subQ0]),TDD([makeQuery(id+"F0.imprint","IMPRINT",EDGE,{"disambiguationData":[TD([[makeQuery(id+"F0.imprint","INTERSECT",VERTEX,{"derivedFrom":[subQ0,sQuery(id+"F0.wireOp",EDGE,"E13")]}),1.0]])],"derivedFrom":subQ0})])]}),makeQuery(id+"F7.opExtrude","SWEPT_FACE",FACE,{"disambiguationData":[OSD([subQ0]),TDD([makeQuery(id+"F0.imprint","IMPRINT",EDGE,{"disambiguationData":[TD([[makeQuery(id+"F0.imprint","INTERSECT",VERTEX,{"derivedFrom":[subQ0,sQuery(id+"F0.wireOp",EDGE,"E9")]}),-1.0]])],"derivedFrom":subQ0})])]}),makeQuery(id+"F7.opExtrude","SWEPT_FACE",FACE,{"disambiguationData":[OSD([subQ0]),TDD([makeQuery(id+"F0.imprint","IMPRINT",EDGE,{"disambiguationData":[TD([[makeQuery(id+"F0.imprint","INTERSECT",VERTEX,{"derivedFrom":[subQ0,sQuery(id+"F0.wireOp",EDGE,"E52")]}),1.0]])],"derivedFrom":subQ0})])]}),makeQuery(id+"F7.opExtrude","SWEPT_FACE",FACE,{"disambiguationData":[OSD([subQ0]),TDD([makeQuery(id+"F0.imprint","IMPRINT",EDGE,{"disambiguationData":[TD([[makeQuery(id+"F0.imprint","INTERSECT",VERTEX,{"derivedFrom":[subQ0,sQuery(id+"F0.wireOp",EDGE,"E50")]}),-1.0]])],"derivedFrom":subQ0})])]}),makeQuery(id+"F7.opExtrude","SWEPT_FACE",FACE,{"disambiguationData":[OSD([subQ0]),TDD([makeQuery(id+"F0.imprint","IMPRINT",EDGE,{"disambiguationData":[TD([[makeQuery(id+"F0.imprint","INTERSECT",VERTEX,{"derivedFrom":[subQ0,sQuery(id+"F0.wireOp",EDGE,"E31")]}),1.0]])],"derivedFrom":subQ0})])]}),makeQuery(id+"F7.opExtrude","SWEPT_FACE",FACE,{"disambiguationData":[OSD([subQ0]),TDD([makeQuery(id+"F0.imprint","IMPRINT",EDGE,{"disambiguationData":[TD([[makeQuery(id+"F0.imprint","INTERSECT",VERTEX,{"derivedFrom":[subQ0,sQuery(id+"F0.wireOp",EDGE,"E33")]}),-1.0]])],"derivedFrom":subQ0})])]})]})],"blendedInto":[makeQuery(id+"F7.boolean.opBoolean","MERGE",FACE,{"derivedFrom":[makeQuery(id+"F6.opExtrude","SWEPT_FACE",FACE,{"disambiguationData":[OSD([sQuery(id+"F1.wireOp",EDGE,"E89")])]}),makeQuery(id+"F7.opExtrude","SWEPT_FACE",FACE,{"disambiguationData":[OSD([subQ0]),TDD([makeQuery(id+"F0.imprint","IMPRINT",EDGE,{"disambiguationData":[TD([[makeQuery(id+"F0.imprint","INTERSECT",VERTEX,{"derivedFrom":[subQ0,sQuery(id+"F0.wireOp",EDGE,"E47")]}),-1.0]])],"derivedFrom":subQ0})])]}),makeQuery(id+"F7.opExtrude","SWEPT_FACE",FACE,{"disambiguationData":[OSD([subQ0]),TDD([makeQuery(id+"F0.imprint","IMPRINT",EDGE,{"disambiguationData":[TD([[makeQuery(id+"F0.imprint","INTERSECT",VERTEX,{"derivedFrom":[subQ0,sQuery(id+"F0.wireOp",EDGE,"E75")]}),-1.0]])],"derivedFrom":subQ0}),makeQuery(id+"F0.imprint","IMPRINT",EDGE,{"disambiguationData":[TD([[subQ2,-1.0]])],"derivedFrom":subQ0})])]}),makeQuery(id+"F7.opExtrude","SWEPT_FACE",FACE,{"disambiguationData":[OSD([subQ0]),TDD([subQ1])]}),makeQuery(id+"F7.opExtrude","SWEPT_FACE",FACE,{"disambiguationData":[OSD([subQ0]),TDD([makeQuery(id+"F0.imprint","IMPRINT",EDGE,{"disambiguationData":[TD([[makeQuery(id+"F0.imprint","INTERSECT",VERTEX,{"derivedFrom":[subQ0,sQuery(id+"F0.wireOp",EDGE,"E13")]}),1.0]])],"derivedFrom":subQ0})])]}),makeQuery(id+"F7.opExtrude","SWEPT_FACE",FACE,{"disambiguationData":[OSD([subQ0]),TDD([makeQuery(id+"F0.imprint","IMPRINT",EDGE,{"disambiguationData":[TD([[makeQuery(id+"F0.imprint","INTERSECT",VERTEX,{"derivedFrom":[subQ0,sQuery(id+"F0.wireOp",EDGE,"E9")]}),-1.0]])],"derivedFrom":subQ0})])]}),makeQuery(id+"F7.opExtrude","SWEPT_FACE",FACE,{"disambiguationData":[OSD([subQ0]),TDD([makeQuery(id+"F0.imprint","IMPRINT",EDGE,{"disambiguationData":[TD([[makeQuery(id+"F0.imprint","INTERSECT",VERTEX,{"derivedFrom":[subQ0,sQuery(id+"F0.wireOp",EDGE,"E52")]}),1.0]])],"derivedFrom":subQ0})])]}),makeQuery(id+"F7.opExtrude","SWEPT_FACE",FACE,{"disambiguationData":[OSD([subQ0]),TDD([makeQuery(id+"F0.imprint","IMPRINT",EDGE,{"disambiguationData":[TD([[makeQuery(id+"F0.imprint","INTERSECT",VERTEX,{"derivedFrom":[subQ0,sQuery(id+"F0.wireOp",EDGE,"E50")]}),-1.0]])],"derivedFrom":subQ0})])]}),makeQuery(id+"F7.opExtrude","SWEPT_FACE",FACE,{"disambiguationData":[OSD([subQ0]),TDD([makeQuery(id+"F0.imprint","IMPRINT",EDGE,{"disambiguationData":[TD([[makeQuery(id+"F0.imprint","INTERSECT",VERTEX,{"derivedFrom":[subQ0,sQuery(id+"F0.wireOp",EDGE,"E31")]}),1.0]])],"derivedFrom":subQ0})])]}),makeQuery(id+"F7.opExtrude","SWEPT_FACE",FACE,{"disambiguationData":[OSD([subQ0]),TDD([makeQuery(id+"F0.imprint","IMPRINT",EDGE,{"disambiguationData":[TD([[makeQuery(id+"F0.imprint","INTERSECT",VERTEX,{"derivedFrom":[subQ0,sQuery(id+"F0.wireOp",EDGE,"E33")]}),-1.0]])],"derivedFrom":subQ0})])]})]})]});}
            var Q28;
            {var subQ0=sQuery(id+"F0.wireOp",EDGE,"E0");var subQ1=makeQuery(id+"F0.imprint","IMPRINT",EDGE,{"disambiguationData":[TD([[makeQuery(id+"F0.imprint","INTERSECT",VERTEX,{"derivedFrom":[subQ0,sQuery(id+"F0.wireOp",EDGE,"E33")]}),-1.0]])],"derivedFrom":subQ0});var subQ2=makeQuery(id+"F0.imprint","INTERSECT",VERTEX,{"derivedFrom":[subQ0,sQuery(id+"F0.wireOp",EDGE,"E69")]});Q28=makeQuery(id+"F8.opChamfer","BLEND_EDGE",EDGE,{"disambiguationData":[OD(2.0)],"blendedFrom":[makeQuery(id+"F7.opExtrude","CAP_EDGE",EDGE,{"disambiguationData":[OSD([subQ0]),TDD([subQ1])],"isStart":false}),makeQuery(id+"F7.boolean.opBoolean","MERGE",FACE,{"derivedFrom":[makeQuery(id+"F6.opExtrude","SWEPT_FACE",FACE,{"disambiguationData":[OSD([sQuery(id+"F1.wireOp",EDGE,"E89")])]}),makeQuery(id+"F7.opExtrude","SWEPT_FACE",FACE,{"disambiguationData":[OSD([subQ0]),TDD([makeQuery(id+"F0.imprint","IMPRINT",EDGE,{"disambiguationData":[TD([[makeQuery(id+"F0.imprint","INTERSECT",VERTEX,{"derivedFrom":[subQ0,sQuery(id+"F0.wireOp",EDGE,"E47")]}),-1.0]])],"derivedFrom":subQ0})])]}),makeQuery(id+"F7.opExtrude","SWEPT_FACE",FACE,{"disambiguationData":[OSD([subQ0]),TDD([makeQuery(id+"F0.imprint","IMPRINT",EDGE,{"disambiguationData":[TD([[makeQuery(id+"F0.imprint","INTERSECT",VERTEX,{"derivedFrom":[subQ0,sQuery(id+"F0.wireOp",EDGE,"E75")]}),-1.0]])],"derivedFrom":subQ0}),makeQuery(id+"F0.imprint","IMPRINT",EDGE,{"disambiguationData":[TD([[subQ2,-1.0]])],"derivedFrom":subQ0})])]}),makeQuery(id+"F7.opExtrude","SWEPT_FACE",FACE,{"disambiguationData":[OSD([subQ0]),TDD([makeQuery(id+"F0.imprint","IMPRINT",EDGE,{"disambiguationData":[TD([[makeQuery(id+"F0.imprint","INTERSECT",VERTEX,{"derivedFrom":[subQ0,sQuery(id+"F0.wireOp",EDGE,"E81")]}),-1.0]])],"derivedFrom":subQ0})])]}),makeQuery(id+"F7.opExtrude","SWEPT_FACE",FACE,{"disambiguationData":[OSD([subQ0]),TDD([makeQuery(id+"F0.imprint","IMPRINT",EDGE,{"disambiguationData":[TD([[makeQuery(id+"F0.imprint","INTERSECT",VERTEX,{"derivedFrom":[subQ0,sQuery(id+"F0.wireOp",EDGE,"E13")]}),1.0]])],"derivedFrom":subQ0})])]}),makeQuery(id+"F7.opExtrude","SWEPT_FACE",FACE,{"disambiguationData":[OSD([subQ0]),TDD([makeQuery(id+"F0.imprint","IMPRINT",EDGE,{"disambiguationData":[TD([[makeQuery(id+"F0.imprint","INTERSECT",VERTEX,{"derivedFrom":[subQ0,sQuery(id+"F0.wireOp",EDGE,"E9")]}),-1.0]])],"derivedFrom":subQ0})])]}),makeQuery(id+"F7.opExtrude","SWEPT_FACE",FACE,{"disambiguationData":[OSD([subQ0]),TDD([makeQuery(id+"F0.imprint","IMPRINT",EDGE,{"disambiguationData":[TD([[makeQuery(id+"F0.imprint","INTERSECT",VERTEX,{"derivedFrom":[subQ0,sQuery(id+"F0.wireOp",EDGE,"E52")]}),1.0]])],"derivedFrom":subQ0})])]}),makeQuery(id+"F7.opExtrude","SWEPT_FACE",FACE,{"disambiguationData":[OSD([subQ0]),TDD([makeQuery(id+"F0.imprint","IMPRINT",EDGE,{"disambiguationData":[TD([[makeQuery(id+"F0.imprint","INTERSECT",VERTEX,{"derivedFrom":[subQ0,sQuery(id+"F0.wireOp",EDGE,"E50")]}),-1.0]])],"derivedFrom":subQ0})])]}),makeQuery(id+"F7.opExtrude","SWEPT_FACE",FACE,{"disambiguationData":[OSD([subQ0]),TDD([makeQuery(id+"F0.imprint","IMPRINT",EDGE,{"disambiguationData":[TD([[makeQuery(id+"F0.imprint","INTERSECT",VERTEX,{"derivedFrom":[subQ0,sQuery(id+"F0.wireOp",EDGE,"E31")]}),1.0]])],"derivedFrom":subQ0})])]}),makeQuery(id+"F7.opExtrude","SWEPT_FACE",FACE,{"disambiguationData":[OSD([subQ0]),TDD([subQ1])]})]})],"blendedInto":[makeQuery(id+"F7.boolean.opBoolean","MERGE",FACE,{"derivedFrom":[makeQuery(id+"F6.opExtrude","SWEPT_FACE",FACE,{"disambiguationData":[OSD([sQuery(id+"F1.wireOp",EDGE,"E89")])]}),makeQuery(id+"F7.opExtrude","SWEPT_FACE",FACE,{"disambiguationData":[OSD([subQ0]),TDD([makeQuery(id+"F0.imprint","IMPRINT",EDGE,{"disambiguationData":[TD([[makeQuery(id+"F0.imprint","INTERSECT",VERTEX,{"derivedFrom":[subQ0,sQuery(id+"F0.wireOp",EDGE,"E47")]}),-1.0]])],"derivedFrom":subQ0})])]}),makeQuery(id+"F7.opExtrude","SWEPT_FACE",FACE,{"disambiguationData":[OSD([subQ0]),TDD([makeQuery(id+"F0.imprint","IMPRINT",EDGE,{"disambiguationData":[TD([[makeQuery(id+"F0.imprint","INTERSECT",VERTEX,{"derivedFrom":[subQ0,sQuery(id+"F0.wireOp",EDGE,"E75")]}),-1.0]])],"derivedFrom":subQ0}),makeQuery(id+"F0.imprint","IMPRINT",EDGE,{"disambiguationData":[TD([[subQ2,-1.0]])],"derivedFrom":subQ0})])]}),makeQuery(id+"F7.opExtrude","SWEPT_FACE",FACE,{"disambiguationData":[OSD([subQ0]),TDD([makeQuery(id+"F0.imprint","IMPRINT",EDGE,{"disambiguationData":[TD([[makeQuery(id+"F0.imprint","INTERSECT",VERTEX,{"derivedFrom":[subQ0,sQuery(id+"F0.wireOp",EDGE,"E81")]}),-1.0]])],"derivedFrom":subQ0})])]}),makeQuery(id+"F7.opExtrude","SWEPT_FACE",FACE,{"disambiguationData":[OSD([subQ0]),TDD([makeQuery(id+"F0.imprint","IMPRINT",EDGE,{"disambiguationData":[TD([[makeQuery(id+"F0.imprint","INTERSECT",VERTEX,{"derivedFrom":[subQ0,sQuery(id+"F0.wireOp",EDGE,"E13")]}),1.0]])],"derivedFrom":subQ0})])]}),makeQuery(id+"F7.opExtrude","SWEPT_FACE",FACE,{"disambiguationData":[OSD([subQ0]),TDD([makeQuery(id+"F0.imprint","IMPRINT",EDGE,{"disambiguationData":[TD([[makeQuery(id+"F0.imprint","INTERSECT",VERTEX,{"derivedFrom":[subQ0,sQuery(id+"F0.wireOp",EDGE,"E9")]}),-1.0]])],"derivedFrom":subQ0})])]}),makeQuery(id+"F7.opExtrude","SWEPT_FACE",FACE,{"disambiguationData":[OSD([subQ0]),TDD([makeQuery(id+"F0.imprint","IMPRINT",EDGE,{"disambiguationData":[TD([[makeQuery(id+"F0.imprint","INTERSECT",VERTEX,{"derivedFrom":[subQ0,sQuery(id+"F0.wireOp",EDGE,"E52")]}),1.0]])],"derivedFrom":subQ0})])]}),makeQuery(id+"F7.opExtrude","SWEPT_FACE",FACE,{"disambiguationData":[OSD([subQ0]),TDD([makeQuery(id+"F0.imprint","IMPRINT",EDGE,{"disambiguationData":[TD([[makeQuery(id+"F0.imprint","INTERSECT",VERTEX,{"derivedFrom":[subQ0,sQuery(id+"F0.wireOp",EDGE,"E50")]}),-1.0]])],"derivedFrom":subQ0})])]}),makeQuery(id+"F7.opExtrude","SWEPT_FACE",FACE,{"disambiguationData":[OSD([subQ0]),TDD([makeQuery(id+"F0.imprint","IMPRINT",EDGE,{"disambiguationData":[TD([[makeQuery(id+"F0.imprint","INTERSECT",VERTEX,{"derivedFrom":[subQ0,sQuery(id+"F0.wireOp",EDGE,"E31")]}),1.0]])],"derivedFrom":subQ0})])]}),makeQuery(id+"F7.opExtrude","SWEPT_FACE",FACE,{"disambiguationData":[OSD([subQ0]),TDD([subQ1])]})]})]});}
            fillet(context, id + "F10", {"entities" : qUnion([Q0, Q1, Q2, Q3, Q4, Q5, Q6, Q7, Q8, Q9, Q10, Q11, Q12, Q13, Q14, Q15, Q16, Q17, Q18, Q19, Q20, Q21, Q22, Q23, Q24, Q25, Q26, Q27, Q28]), "radius" : 5 * mm, "tangentPropagation" : true, "allowEdgeOverflow" : false});
        }
    });
